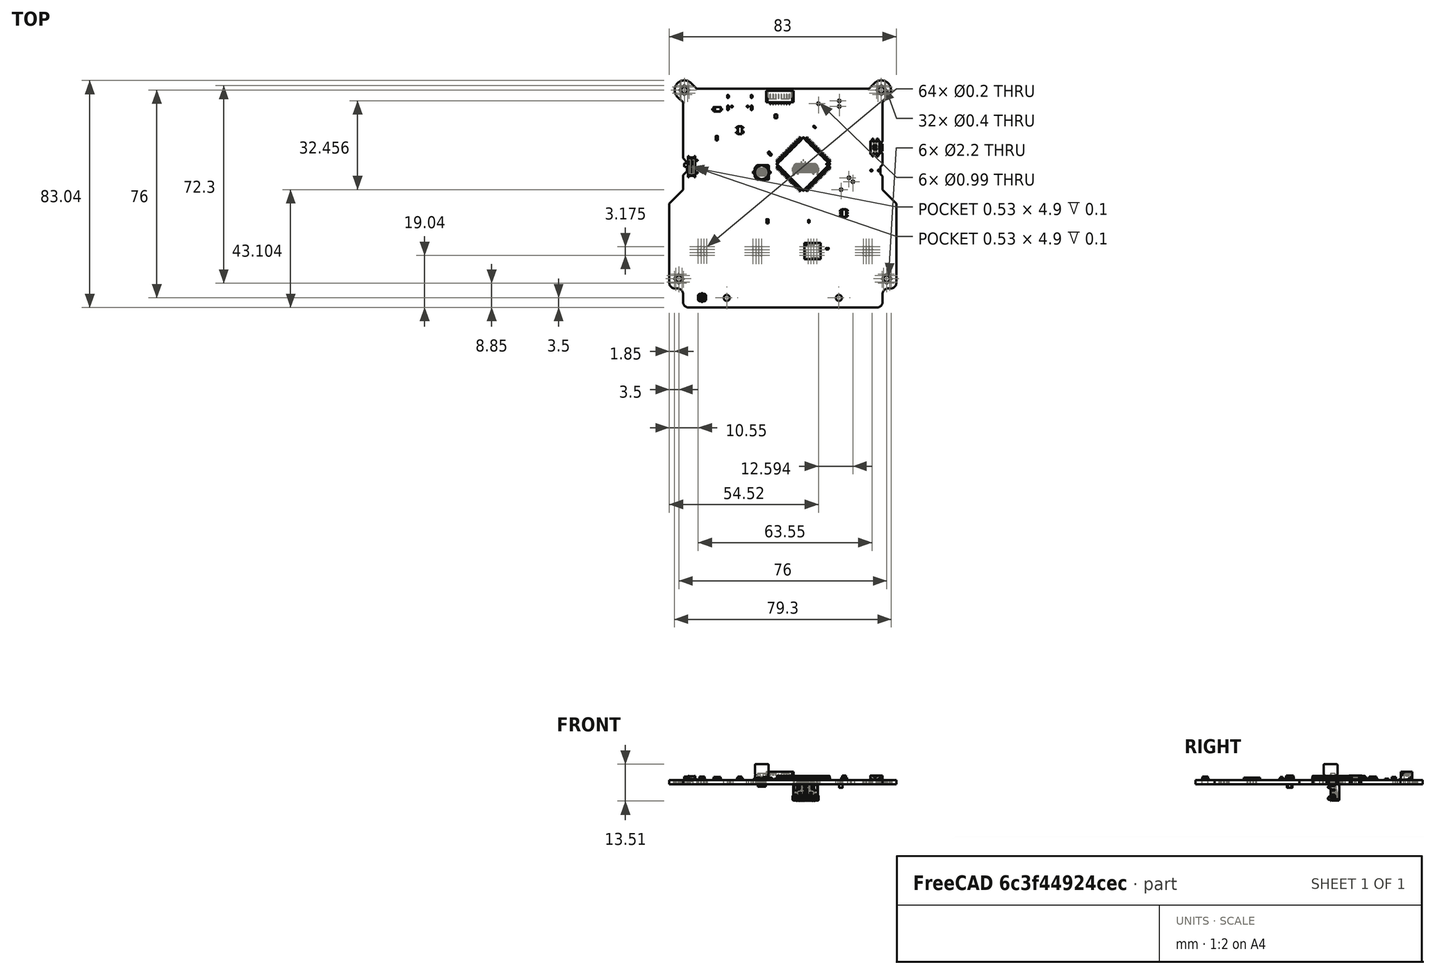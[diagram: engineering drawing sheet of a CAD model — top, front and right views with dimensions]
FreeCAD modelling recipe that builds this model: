
FCSTD DOCUMENT  (FreeCAD 0.20R29410 (Git))
Label: ReLoki_PCB
License: All rights reserved
LicenseURL: http://en.wikipedia.org/wiki/All_rights_reserved
objects: App::Link×261, Part::Feature×83, App::Part×14, PartDesign::CoordinateSystem×1, Sketcher::SketchObject×1
note: 85 computed .brp shape members not serialized (recipe doc carries the construction recipe); baked Part::Feature solids carry a one-line shape summary decoded from their .brp

FEATURE [PartDesign::CoordinateSystem] Local_CS_b912
  AttacherType = Attacher::AttachEngine3D
  MapMode = 2
  Support = -> [X_Axis001]
FEATURE [Part::Feature] Pcb_b912
  Placement = pos=(-58.8,135.6,0) rot=(0,0,1;0rad)
  shape: bbox 83 x 83.04 x 1.58 mm, 187 faces (baked)
FEATURE [Sketcher::SketchObject] PCB_Sketch_b912
  FullyConstrained = false
  sketch-geometry (36):
    g0: LineSegment StartX=43.35 StartY=2 StartZ=0 EndX=43.35 EndY=-0.599999 EndZ=0
    g1: LineSegment StartX=44.2 StartY=6.95 StartZ=0 EndX=44.2 EndY=2.85 EndZ=0
    g2: LineSegment StartX=43.35 StartY=10.4 StartZ=0 EndX=44.2 EndY=11.25 EndZ=0
    g3: LineSegment StartX=43.35 StartY=2 StartZ=0 EndX=44.2 EndY=2.85 EndZ=0
    g4: LineSegment StartX=49.2 StartY=-11.4 StartZ=0 EndX=44.2 EndY=-6.4 EndZ=0
    g5: LineSegment StartX=44.2 StartY=-1.45 StartZ=0 EndX=44.2 EndY=-6.4 EndZ=0
    g6: LineSegment StartX=43.35 StartY=-0.599999 StartZ=0 EndX=44.2 EndY=-1.45 EndZ=0
    g7: LineSegment StartX=-28.8 StartY=-6.4 StartZ=0 EndX=-28.8 EndY=-1.05 EndZ=0
    g8: LineSegment StartX=-23.8 StartY=30.6 StartZ=0 EndX=-25.8 EndY=32.6 EndZ=0
    g9: LineSegment StartX=-33.8 StartY=-11.4 StartZ=0 EndX=-33.8 EndY=-40.4 EndZ=0
    g10: LineSegment StartX=39.2 StartY=30.6 StartZ=0 EndX=41.2 EndY=32.6 EndZ=0
    g11: LineSegment StartX=-33.8 StartY=-11.4 StartZ=0 EndX=-28.8 EndY=-6.4 EndZ=0
    g12: LineSegment StartX=49.2 StartY=-11.4 StartZ=0 EndX=49.2 EndY=-40.4 EndZ=0
    g13: LineSegment StartX=43.35 StartY=10.4 StartZ=0 EndX=43.35 EndY=7.8 EndZ=0
    g14: LineSegment StartX=46.2 StartY=27.6 StartZ=0 EndX=44.2 EndY=25.6 EndZ=0
    g15: LineSegment StartX=-27.3 StartY=3.75 StartZ=0 EndX=-28.8 EndY=5.25 EndZ=0
    g16: LineSegment StartX=-30.8 StartY=-42.4 StartZ=0 EndX=-31.8 EndY=-42.4 EndZ=0
    g17: LineSegment StartX=-23.8 StartY=30.6 StartZ=0 EndX=39.2 EndY=30.6 EndZ=0
    g18: LineSegment StartX=-28.8 StartY=-47.4 StartZ=0 EndX=-28.8 EndY=-44.4 EndZ=0
    g19: LineSegment StartX=-27.3 StartY=0.450001 StartZ=0 EndX=-28.8 EndY=-1.05 EndZ=0
    g20: LineSegment StartX=44.2 StartY=-47.4 StartZ=0 EndX=44.2 EndY=-44.4 EndZ=0
    g21: LineSegment StartX=44.2 StartY=11.25 StartZ=0 EndX=44.2 EndY=25.6 EndZ=0
    g22: LineSegment StartX=-27.3 StartY=3.75 StartZ=0 EndX=-27.3 EndY=0.450001 EndZ=0
    g23: LineSegment StartX=42.2 StartY=-49.4 StartZ=0 EndX=-26.8 EndY=-49.4 EndZ=0
    g24: LineSegment StartX=43.35 StartY=7.8 StartZ=0 EndX=44.2 EndY=6.95 EndZ=0
    g25: LineSegment StartX=-28.8 StartY=25.6 StartZ=0 EndX=-30.8 EndY=27.6 EndZ=0
    g26: LineSegment StartX=47.2 StartY=-42.4 StartZ=0 EndX=46.2 EndY=-42.4 EndZ=0
    g27: LineSegment StartX=-28.8 StartY=5.25 StartZ=0 EndX=-28.8 EndY=25.6 EndZ=0
    g28: ArcOfCircle CenterX=47.2 CenterY=-40.4 CenterZ=0 NormalX=0 NormalY=0 NormalZ=-1 AngleXU=3.14159 Radius=2 StartAngle=0 EndAngle=1.5708
    g29: ArcOfCircle CenterX=-26.8 CenterY=-47.4 CenterZ=0 NormalX=0 NormalY=0 NormalZ=-1 AngleXU=-1.5708 Radius=2 StartAngle=0 EndAngle=1.5708
    g30: ArcOfCircle CenterX=-28.3 CenterY=30.1 CenterZ=0 NormalX=0 NormalY=0 NormalZ=-1 AngleXU=-0.785398 Radius=3.53553 StartAngle=0 EndAngle=3.14159
    g31: ArcOfCircle CenterX=42.2 CenterY=-47.4 CenterZ=0 NormalX=0 NormalY=0 NormalZ=-1 AngleXU=3.14159 Radius=2 StartAngle=0 EndAngle=1.5708
    g32: ArcOfCircle CenterX=-31.8 CenterY=-40.4 CenterZ=0 NormalX=0 NormalY=0 NormalZ=-1 AngleXU=-1.5708 Radius=2 StartAngle=0 EndAngle=1.5708
    g33: ArcOfCircle CenterX=46.2 CenterY=-44.4 CenterZ=0 NormalX=0 NormalY=0 NormalZ=-1 AngleXU=-7.47076e-07 Radius=2 StartAngle=0 EndAngle=1.5708
    g34: ArcOfCircle CenterX=43.7 CenterY=30.1 CenterZ=0 NormalX=0 NormalY=0 NormalZ=-1 AngleXU=0.785398 Radius=3.53553 StartAngle=0 EndAngle=3.14159
    g35: ArcOfCircle CenterX=-30.8 CenterY=-44.4 CenterZ=0 NormalX=0 NormalY=0 NormalZ=-1 AngleXU=1.5708 Radius=2 StartAngle=0 EndAngle=1.5708
  constraints (36):
    c: Coincident(g9,g32)
    c: Coincident(g9,g11)
    c: Coincident(g16,g32)
    c: Coincident(g16,g35)
    c: Coincident(g25,g30)
    c: Coincident(g18,g29)
    c: Coincident(g18,g35)
    c: Coincident(g7,g11)
    c: Coincident(g7,g19)
    c: Coincident(g15,g27)
    c: Coincident(g25,g27)
    c: Coincident(g19,g22)
    c: Coincident(g15,g22)
    c: Coincident(g23,g29)
    c: Coincident(g8,g30)
    c: Coincident(g8,g17)
    c: Coincident(g10,g17)
    c: Coincident(g10,g34)
    c: Coincident(g23,g31)
    c: Coincident(g0,g6)
    c: Coincident(g0,g3)
    c: Coincident(g13,g24)
    c: Coincident(g2,g13)
    c: Coincident(g20,g31)
    c: Coincident(g20,g33)
    c: Coincident(g4,g5)
    c: Coincident(g5,g6)
    c: Coincident(g1,g3)
    c: Coincident(g1,g24)
    c: Coincident(g2,g21)
    c: Coincident(g14,g21)
    c: Coincident(g26,g33)
    c: Coincident(g14,g34)
    c: Coincident(g26,g28)
    c: Coincident(g12,g28)
    c: Coincident(g4,g12)
FEATURE [Part::Feature] Shape  label="R14_R_0402_1005Metric_de650128e65b"
  Placement = pos=(17.2,-17.91,0) rot=(0,0,-1;1.5708rad)
  shape: bbox 0.5 x 1 x 0.35 mm, 26 faces (baked)
FEATURE [Part::Feature] Shape001  label="C81_C_0402_1005Metric_8f684d3886a5"
  Placement = pos=(24,-27.92,0) rot=(0,0,1;0rad)
  shape: bbox 1 x 0.5 x 0.5 mm, 28 faces (baked)
FEATURE [App::Link] R14_R_0402_1005Metric_de650128e65b_ln_  label="R74_R_0402_1005Metric_a4a14273bc81"
  LinkPlacement = pos=(6.5,-7.7,0) rot=(0,0,-1;0.785398rad)
  LinkedObject = -> Shape
  Placement = pos=(6.5,-7.7,0) rot=(0,0,-1;0.785398rad)
FEATURE [App::Link] R14_R_0402_1005Metric_de650128e65b_ln_001  label="R54_R_0402_1005Metric_1bb991507df9"
  LinkPlacement = pos=(5.075,-17.885,0) rot=(0,0,-1;1.5708rad)
  LinkedObject = -> Shape
  Placement = pos=(5.075,-17.885,0) rot=(0,0,-1;1.5708rad)
FEATURE [Part::Feature] Shape002  label="U1_LQFP_100_14x14mm_P05mm_23f8fdaca507"
  Placement = pos=(15.2,3.01585,0) rot=(0,0,1;3.92699rad)
  shape: bbox 19.95 x 19.95 x 1.5 mm, 1544 faces (baked)
FEATURE [App::Link] C81_C_0402_1005Metric_8f684d3886a5_ln_  label="C65_C_0402_1005Metric_c0867cacedee"
  LinkPlacement = pos=(21.01,-34.68,0) rot=(0,0,-1;1.5708rad)
  LinkedObject = -> Shape001
  Placement = pos=(21.01,-34.68,0) rot=(0,0,-1;1.5708rad)
FEATURE [App::Link] C81_C_0402_1005Metric_8f684d3886a5_ln_001  label="C141_C_0402_1005Metric_d101c3108a75"
  LinkPlacement = pos=(-20.925,-23.39,0) rot=(0,0,1;1.5708rad)
  LinkedObject = -> Shape001
  Placement = pos=(-20.925,-23.39,0) rot=(0,0,1;1.5708rad)
FEATURE [App::Link] R14_R_0402_1005Metric_de650128e65b_ln_002  label="R76_R_0402_1005Metric_5a17da7a795e"
  LinkPlacement = pos=(8.5,-14.57,0) rot=(0,0,1;1.5708rad)
  LinkedObject = -> Shape
  Placement = pos=(8.5,-14.57,0) rot=(0,0,1;1.5708rad)
FEATURE [App::Link] R14_R_0402_1005Metric_de650128e65b_ln_003  label="R45_R_0402_1005Metric_9db44bebc8a2"
  LinkPlacement = pos=(37.05,-23.375,0) rot=(0,0,1;1.5708rad)
  LinkedObject = -> Shape
  Placement = pos=(37.05,-23.375,0) rot=(0,0,1;1.5708rad)
FEATURE [App::Link] R14_R_0402_1005Metric_de650128e65b_ln_004  label="R30_R_0402_1005Metric_54cea338f5d0"
  LinkPlacement = pos=(33.8625,14.25,0) rot=(0,0,1;3.14159rad)
  LinkedObject = -> Shape
  Placement = pos=(33.8625,14.25,0) rot=(0,0,1;3.14159rad)
FEATURE [App::Link] R14_R_0402_1005Metric_de650128e65b_ln_005  label="R80_R_0402_1005Metric_603352afcd9c"
  LinkPlacement = pos=(28.9375,-17.86,0) rot=(0,0,-1;1.5708rad)
  LinkedObject = -> Shape
  Placement = pos=(28.9375,-17.86,0) rot=(0,0,-1;1.5708rad)
FEATURE [Part::Feature] Shape003  label="D13_LED_0603_1608Metric_a9e6ce14452c"
  Placement = pos=(2.075,-17.92,0) rot=(0,0,-1;1.5708rad)
  shape: bbox 0.8 x 1.6 x 1.1 mm, 50 faces (baked)
FEATURE [App::Link] R14_R_0402_1005Metric_de650128e65b_ln_006  label="R25_R_0402_1005Metric_f967b688b800"
  LinkPlacement = pos=(33.8625,16.85,0) rot=(0,0,1;3.14159rad)
  LinkedObject = -> Shape
  Placement = pos=(33.8625,16.85,0) rot=(0,0,1;3.14159rad)
FEATURE [App::Link] C81_C_0402_1005Metric_8f684d3886a5_ln_002  label="C127_C_0402_1005Metric_1b485c7792d8"
  LinkPlacement = pos=(-21.25,-34.67,0) rot=(0,0,-1;1.5708rad)
  LinkedObject = -> Shape001
  Placement = pos=(-21.25,-34.67,0) rot=(0,0,-1;1.5708rad)
FEATURE [App::Link] D13_LED_0603_1608Metric_a9e6ce14452c_ln_  label="D14_LED_0603_1608Metric_ef9f26dd3791"
  LinkPlacement = pos=(0.374999,-17.92,0) rot=(0,0,-1;1.5708rad)
  LinkedObject = -> Shape003
  Placement = pos=(0.374999,-17.92,0) rot=(0,0,-1;1.5708rad)
FEATURE [App::Link] C81_C_0402_1005Metric_8f684d3886a5_ln_003  label="C17_C_0402_1005Metric_0b858d9f6a69"
  LinkPlacement = pos=(22.3394,11.9894,0) rot=(0,0,1;0.785398rad)
  LinkedObject = -> Shape001
  Placement = pos=(22.3394,11.9894,0) rot=(0,0,1;0.785398rad)
FEATURE [App::Link] R14_R_0402_1005Metric_de650128e65b_ln_007  label="R8_R_0402_1005Metric_1ff775f01767"
  LinkPlacement = pos=(34.775,-17.91,0) rot=(0,0,1;1.5708rad)
  LinkedObject = -> Shape
  Placement = pos=(34.775,-17.91,0) rot=(0,0,1;1.5708rad)
FEATURE [App::Link] C81_C_0402_1005Metric_8f684d3886a5_ln_004  label="C102_C_0402_1005Metric_637c617e709d"
  LinkPlacement = pos=(0.324999,-33.2,0) rot=(0,0,1;0rad)
  LinkedObject = -> Shape001
  Placement = pos=(0.324999,-33.2,0) rot=(0,0,1;0rad)
FEATURE [App::Link] D13_LED_0603_1608Metric_a9e6ce14452c_ln_001  label="D10_LED_0603_1608Metric_a73bad670425"
  LinkPlacement = pos=(40.65,-17.9325,0) rot=(0,0,-1;1.5708rad)
  LinkedObject = -> Shape003
  Placement = pos=(40.65,-17.9325,0) rot=(0,0,-1;1.5708rad)
FEATURE [App::Link] C81_C_0402_1005Metric_8f684d3886a5_ln_005  label="C28_C_0402_1005Metric_d3135e10789d"
  LinkPlacement = pos=(9.75204,-6.68211,0) rot=(0,0,1;3.92699rad)
  LinkedObject = -> Shape001
  Placement = pos=(9.75204,-6.68211,0) rot=(0,0,1;3.92699rad)
FEATURE [App::Link] R14_R_0402_1005Metric_de650128e65b_ln_008  label="R2_R_0402_1005Metric_00b5c8fd95a4"
  LinkPlacement = pos=(34.1725,23,0) rot=(0,0,1;3.14159rad)
  LinkedObject = -> Shape
  Placement = pos=(34.1725,23,0) rot=(0,0,1;3.14159rad)
FEATURE [App::Link] R14_R_0402_1005Metric_de650128e65b_ln_009  label="R63_R_0402_1005Metric_3ae226b5d65f"
  LinkPlacement = pos=(-27.375,-28.495,0) rot=(0,0,1;1.5708rad)
  LinkedObject = -> Shape
  Placement = pos=(-27.375,-28.495,0) rot=(0,0,1;1.5708rad)
FEATURE [App::Link] C81_C_0402_1005Metric_8f684d3886a5_ln_006  label="C149_C_0402_1005Metric_444c0c827598"
  LinkPlacement = pos=(26.7375,-13.75,0) rot=(0,0,1;3.14159rad)
  LinkedObject = -> Shape001
  Placement = pos=(26.7375,-13.75,0) rot=(0,0,1;3.14159rad)
FEATURE [App::Link] R14_R_0402_1005Metric_de650128e65b_ln_010  label="R50_R_0402_1005Metric_d7a9ffa530aa"
  LinkPlacement = pos=(11.235,-24.56,0) rot=(0,0,1;3.14159rad)
  LinkedObject = -> Shape
  Placement = pos=(11.235,-24.56,0) rot=(0,0,1;3.14159rad)
FEATURE [App::Link] R14_R_0402_1005Metric_de650128e65b_ln_011  label="R46_R_0402_1005Metric_4825f84f8d7c"
  LinkPlacement = pos=(25.15,-17.88,0) rot=(0,0,-1;1.5708rad)
  LinkedObject = -> Shape
  Placement = pos=(25.15,-17.88,0) rot=(0,0,-1;1.5708rad)
FEATURE [App::Link] C81_C_0402_1005Metric_8f684d3886a5_ln_007  label="C73_C_0402_1005Metric_c875b8a4be27"
  LinkPlacement = pos=(24,-31.6,0) rot=(0,0,1;0rad)
  LinkedObject = -> Shape001
  Placement = pos=(24,-31.6,0) rot=(0,0,1;0rad)
FEATURE [App::Link] C81_C_0402_1005Metric_8f684d3886a5_ln_008  label="C134_C_0402_1005Metric_39d0dd4ab5a3"
  LinkPlacement = pos=(-16.2,-30.56,0) rot=(0,0,1;0rad)
  LinkedObject = -> Shape001
  Placement = pos=(-16.2,-30.56,0) rot=(0,0,1;0rad)
FEATURE [App::Link] C81_C_0402_1005Metric_8f684d3886a5_ln_009  label="C151_C_0402_1005Metric_d977a6f65422"
  LinkPlacement = pos=(8.31059,10.9394,0) rot=(0,0,1;2.35619rad)
  LinkedObject = -> Shape001
  Placement = pos=(8.31059,10.9394,0) rot=(0,0,1;2.35619rad)
FEATURE [Part::Feature] Shape004  label="D18_SOT_143_b0c1ef25a24b"
  Placement = pos=(-8.03,15.4398,0) rot=(0,0,1;3.14159rad)
  shape: bbox 2.8 x 2.9 x 1.2 mm, 94 faces (baked)
FEATURE [App::Link] R14_R_0402_1005Metric_de650128e65b_ln_012  label="R57_R_0402_1005Metric_3c6d5dbffcd9"
  LinkPlacement = pos=(-9.325,-32.96,0) rot=(0,0,1;1.5708rad)
  LinkedObject = -> Shape
  Placement = pos=(-9.325,-32.96,0) rot=(0,0,1;1.5708rad)
FEATURE [Part::Feature] Shape005  label="C11_C_0603_1608Metric_4ead5bbb98ed"
  Placement = pos=(-16.45,12.525,0) rot=(0,0,1;1.5708rad)
  shape: bbox 0.8 x 1.6 x 0.8 mm, 28 faces (baked)
FEATURE [Part::Feature] Shape006  label="D20_SOT_886_1dd8b907bd9e"
  Placement = pos=(5.16,20.4898,0) rot=(0,0,1;3.14159rad)
  shape: bbox 1 x 1.45 x 0.52 mm, 38 faces (baked)
FEATURE [Part::Feature] Part__Feature  label="part"
  shape: bbox 0.1003 x 0.1003 x 0.003 mm, 3 faces (baked)
FEATURE [Part::Feature] Part__Feature001  label="part001"
  shape: bbox 2.006 x 1.194 x 0.654 mm, 6 faces (baked)
FEATURE [Part::Feature] Part__Feature002  label="part002"
  shape: bbox 0.508 x 0.99 x 0.006 mm, 6 faces (baked)
FEATURE [Part::Feature] Part__Feature003  label="part003"
  shape: bbox 0.508 x 0.99 x 0.006 mm, 6 faces (baked)
FEATURE [App::Part] part  label="Y2_part004_ffd9eb1ad46b[2]"
  Group = -> [Part__Feature,Part__Feature001,Part__Feature002,Part__Feature003]
  Origin = -> Origin008
  Placement = pos=(3.84444,-0.965614,0) rot=(0,0,1;2.35619rad)
FEATURE [App::Link] C81_C_0402_1005Metric_8f684d3886a5_ln_010  label="C146_C_0402_1005Metric_f6a4e29ba07c"
  LinkPlacement = pos=(9.65,-14.57,0) rot=(0,0,1;1.5708rad)
  LinkedObject = -> Shape001
  Placement = pos=(9.65,-14.57,0) rot=(0,0,1;1.5708rad)
FEATURE [App::Link] C81_C_0402_1005Metric_8f684d3886a5_ln_011  label="C29_C_0402_1005Metric_72a100fbd820"
  LinkPlacement = pos=(20.1394,14.1894,0) rot=(0,0,1;0.785398rad)
  LinkedObject = -> Shape001
  Placement = pos=(20.1394,14.1894,0) rot=(0,0,1;0.785398rad)
FEATURE [App::Link] C81_C_0402_1005Metric_8f684d3886a5_ln_012  label="C130_C_0402_1005Metric_e2b8032ed5ab"
  LinkPlacement = pos=(-19.775,-33.2,0) rot=(0,0,1;0rad)
  LinkedObject = -> Shape001
  Placement = pos=(-19.775,-33.2,0) rot=(0,0,1;0rad)
FEATURE [App::Link] R14_R_0402_1005Metric_de650128e65b_ln_013  label="R37_R_0402_1005Metric_928ee907d34c"
  LinkPlacement = pos=(-18.875,0.890001,0) rot=(0,0,-1;1.5708rad)
  LinkedObject = -> Shape
  Placement = pos=(-18.875,0.890001,0) rot=(0,0,-1;1.5708rad)
FEATURE [Part::Feature] Part__Feature004  label="NONE"
  Placement = pos=(0,-11.5395,4.33352) rot=(0,1,0;1.5708rad)
  shape: bbox 9.583 x 4.163 x 7.533 mm, 1427 faces (baked)
FEATURE [Part::Feature] Part__Feature005  label="ÇÐ³ý-À­Éì2"
  Placement = pos=(0,-11.5395,4.33352) rot=(0,1,0;1.5708rad)
  shape: bbox 7.055 x 2.035 x 7.135 mm, 548 faces (baked)
FEATURE [App::Part] USB4105_15_A  label="J7_USB4105-15-A_0d4446cf3e35[2]"
  Group = -> [Part__Feature004,Part__Feature005]
  Origin = -> Origin009
  Placement = pos=(7.97,30.4098,0) rot=(0,0.707107,0.707107;3.14159rad)
FEATURE [App::Link] C11_C_0603_1608Metric_4ead5bbb98ed_ln_  label="C117_C_0603_1608Metric_39bd58f4b52f"
  LinkPlacement = pos=(-17.85,-34.735,0) rot=(0,0,-1;1.5708rad)
  LinkedObject = -> Shape005
  Placement = pos=(-17.85,-34.735,0) rot=(0,0,-1;1.5708rad)
FEATURE [App::Link] D13_LED_0603_1608Metric_a9e6ce14452c_ln_002  label="D2_LED_0603_1608Metric_1ebbf72df7e2"
  LinkPlacement = pos=(36.9125,23,0) rot=(0,0,1;0rad)
  LinkedObject = -> Shape003
  Placement = pos=(36.9125,23,0) rot=(0,0,1;0rad)
FEATURE [App::Link] C81_C_0402_1005Metric_8f684d3886a5_ln_013  label="C9_C_0402_1005Metric_4d000169be0c"
  LinkPlacement = pos=(2.75,-3.05,0) rot=(0,0,1;0.785398rad)
  LinkedObject = -> Shape001
  Placement = pos=(2.75,-3.05,0) rot=(0,0,1;0.785398rad)
FEATURE [Part::Feature] Shape007  label="SW3_Fusion_sp_02c466c8c368"
  Placement = pos=(-25.3,2.1,0) rot=(0,0,-1;1.5708rad)
  shape: bbox 5 x 7.7 x 2 mm, 141 faces (baked)
FEATURE [App::Link] D13_LED_0603_1608Metric_a9e6ce14452c_ln_003  label="D4_LED_0603_1608Metric_99efae4c4b30"
  LinkPlacement = pos=(36.9125,19.2,0) rot=(0,0,1;0rad)
  LinkedObject = -> Shape003
  Placement = pos=(36.9125,19.2,0) rot=(0,0,1;0rad)
FEATURE [App::Link] R14_R_0402_1005Metric_de650128e65b_ln_014  label="R43_R_0402_1005Metric_da46058e0372"
  LinkPlacement = pos=(42.35,-15.28,0) rot=(0,0,1;1.5708rad)
  LinkedObject = -> Shape
  Placement = pos=(42.35,-15.28,0) rot=(0,0,1;1.5708rad)
FEATURE [App::Link] R14_R_0402_1005Metric_de650128e65b_ln_015  label="R47_R_0402_1005Metric_771e28319039"
  LinkPlacement = pos=(12.85,-28.5,0) rot=(0,0,1;1.5708rad)
  LinkedObject = -> Shape
  Placement = pos=(12.85,-28.5,0) rot=(0,0,1;1.5708rad)
FEATURE [Part::Feature] Shape008  label="SW2_EVQPU-LC-02K v4_ac6ec0e7e283[2]"
  Placement = pos=(41.45,9.1,0) rot=(0.57735,0.57735,0.57735;2.0944rad)
  shape: bbox 4.542 x 6.402 x 2.183 mm, 270 faces (baked)
FEATURE [App::Link] D13_LED_0603_1608Metric_a9e6ce14452c_ln_004  label="D16_LED_0603_1608Metric_2864ecb3f3d8"
  LinkPlacement = pos=(-19.725,-17.92,0) rot=(0,0,-1;1.5708rad)
  LinkedObject = -> Shape003
  Placement = pos=(-19.725,-17.92,0) rot=(0,0,-1;1.5708rad)
FEATURE [App::Link] C81_C_0402_1005Metric_8f684d3886a5_ln_014  label="C88_C_0402_1005Metric_34164e20f501"
  LinkPlacement = pos=(-8.855,-28.96,0) rot=(0,0,1;3.14159rad)
  LinkedObject = -> Shape001
  Placement = pos=(-8.855,-28.96,0) rot=(0,0,1;3.14159rad)
FEATURE [App::Link] R14_R_0402_1005Metric_de650128e65b_ln_016  label="R73_R_0402_1005Metric_d5867035460b"
  LinkPlacement = pos=(-8.59,12.0898,0) rot=(0,0,-1;1.5708rad)
  LinkedObject = -> Shape
  Placement = pos=(-8.59,12.0898,0) rot=(0,0,-1;1.5708rad)
FEATURE [Part::Feature] Shape009  label="U5_QFN40P600X600X90-48_Nordic_Semiconductor_QFN48_2cf8b7c55fc9"
  Placement = pos=(18.525,-28.785,0) rot=(0,0,1;0rad)
  shape: bbox 6.02 x 6.02 x 0.9 mm, 302 faces (baked)
FEATURE [App::Link] R14_R_0402_1005Metric_de650128e65b_ln_017  label="R15_R_0402_1005Metric_1a5054cc167c"
  LinkPlacement = pos=(-2.95,-17.9,0) rot=(0,0,-1;1.5708rad)
  LinkedObject = -> Shape
  Placement = pos=(-2.95,-17.9,0) rot=(0,0,-1;1.5708rad)
FEATURE [App::Link] C81_C_0402_1005Metric_8f684d3886a5_ln_015  label="C86_C_0402_1005Metric_aac071f58c84"
  LinkPlacement = pos=(18.375,-38.03,0) rot=(0,0,-1;1.5708rad)
  LinkedObject = -> Shape001
  Placement = pos=(18.375,-38.03,0) rot=(0,0,-1;1.5708rad)
FEATURE [App::Link] C81_C_0402_1005Metric_8f684d3886a5_ln_016  label="C150_C_0402_1005Metric_d87a535d9fed"
  LinkPlacement = pos=(26,-1.3,0) rot=(0,0,-1;0.785398rad)
  LinkedObject = -> Shape001
  Placement = pos=(26,-1.3,0) rot=(0,0,-1;0.785398rad)
FEATURE [App::Link] R14_R_0402_1005Metric_de650128e65b_ln_018  label="R23_R_0402_1005Metric_31860b2061f3"
  LinkPlacement = pos=(36.3,3.35,0) rot=(0,0,1;0rad)
  LinkedObject = -> Shape
  Placement = pos=(36.3,3.35,0) rot=(0,0,1;0rad)
FEATURE [Part::Feature] Part__Feature006  label="─σ≥αδⁿ"
  shape: bbox 1.5 x 1.5 x 0.5 mm, 6 faces (baked)
FEATURE [Part::Feature] Part__Feature007  label="─σ≥αδⁿ_2"
  Placement = pos=(-0.55,-0.5,0.5) rot=(0,0,1;0rad)
  shape: bbox 0.4 x 0.3 x 0.05 mm, 7 faces (baked)
FEATURE [Part::Feature] Part__Feature008  label="─σ≥αδⁿ_3"
  Placement = pos=(-0.55,-1e-15,0.5) rot=(0,0,1;0rad)
  shape: bbox 0.4 x 0.25 x 0.05 mm, 6 faces (baked)
FEATURE [Part::Feature] Part__Feature009  label="─σ≥αδⁿ_4"
  Placement = pos=(-0.55,0.5,0.5) rot=(0,0,1;0rad)
  shape: bbox 0.4 x 0.3 x 0.05 mm, 6 faces (baked)
FEATURE [Part::Feature] Part__Feature010  label="─σ≥αδⁿ_005"
  Placement = pos=(0.55,-0.5,0.5) rot=(0,0,1;0rad)
  shape: bbox 0.4 x 0.3 x 0.05 mm, 6 faces (baked)
FEATURE [Part::Feature] Part__Feature011  label="─σ≥αδⁿ_006"
  Placement = pos=(0.55,0.5,0.5) rot=(0,0,1;0rad)
  shape: bbox 0.4 x 0.3 x 0.05 mm, 6 faces (baked)
FEATURE [Part::Feature] Part__Feature012  label="─σ≥αδⁿ_007"
  Placement = pos=(0.55,0,0.5) rot=(0,0,1;0rad)
  shape: bbox 0.4 x 0.25 x 0.05 mm, 6 faces (baked)
FEATURE [Part::Feature] Part__Feature013  label="─σ≥αδⁿ_5"
  Placement = pos=(0,-0.525,0.5) rot=(0,0,-1;1.5708rad)
  shape: bbox 0.35 x 0.45 x 0.05 mm, 6 faces (baked)
FEATURE [Part::Feature] Part__Feature014  label="─σ≥αδⁿ_008"
  Placement = pos=(0,0.525,0.5) rot=(0,0,-1;1.5708rad)
  shape: bbox 0.35 x 0.45 x 0.05 mm, 6 faces (baked)
FEATURE [Part::Feature] Part__Feature015  label="─σ≥αδⁿ_6"
  Placement = pos=(-0.5,-0.5,-0.005) rot=(0,0,1;0rad)
  shape: bbox 0.25 x 0.25 x 0.1 mm, 4 faces (baked)
FEATURE [App::Part] User_Library_uqfn8  label="U12_User Library-uqfn8_8f146cca9007"
  Group = -> [Part__Feature006,Part__Feature007,Part__Feature008,Part__Feature009,Part__Feature010,Part__Feature011,Part__Feature012,Part__Feature013,Part__Feature014,Part__Feature015]
  Origin = -> Origin010
  Placement = pos=(-4.45,-7,0.51) rot=(0,1,0;3.14159rad)
FEATURE [Part::Feature] Shape010  label="L1_L_0402_1005Metric_5998b2d09642"
  Placement = pos=(19.302,16.5904,0) rot=(0,0,-1;0.785398rad)
  shape: bbox 1.061 x 1.061 x 0.5 mm, 28 faces (baked)
FEATURE [App::Link] R14_R_0402_1005Metric_de650128e65b_ln_019  label="R60_R_0402_1005Metric_0914d451b9f9"
  LinkPlacement = pos=(0.374999,-15.28,0) rot=(0,0,1;1.5708rad)
  LinkedObject = -> Shape
  Placement = pos=(0.374999,-15.28,0) rot=(0,0,1;1.5708rad)
FEATURE [App::Link] C81_C_0402_1005Metric_8f684d3886a5_ln_017  label="C100_C_0402_1005Metric_557190ddb8d7"
  LinkPlacement = pos=(-7.695,-31.36,0) rot=(0,0,1;3.14159rad)
  LinkedObject = -> Shape001
  Placement = pos=(-7.695,-31.36,0) rot=(0,0,1;3.14159rad)
FEATURE [App::Link] C81_C_0402_1005Metric_8f684d3886a5_ln_018  label="C68_C_0402_1005Metric_135fffc550a4"
  LinkPlacement = pos=(14,-32.915,0) rot=(0,0,1;1.5708rad)
  LinkedObject = -> Shape001
  Placement = pos=(14,-32.915,0) rot=(0,0,1;1.5708rad)
FEATURE [App::Link] C81_C_0402_1005Metric_8f684d3886a5_ln_019  label="C109_C_0402_1005Metric_56ac115547da"
  LinkPlacement = pos=(3.9,-27.92,0) rot=(0,0,1;0rad)
  LinkedObject = -> Shape001
  Placement = pos=(3.9,-27.92,0) rot=(0,0,1;0rad)
FEATURE [App::Link] C81_C_0402_1005Metric_8f684d3886a5_ln_020  label="C69_C_0402_1005Metric_3595023d93e6"
  LinkPlacement = pos=(23.995,-29.3,0) rot=(0,0,1;0rad)
  LinkedObject = -> Shape001
  Placement = pos=(23.995,-29.3,0) rot=(0,0,1;0rad)
FEATURE [App::Link] C81_C_0402_1005Metric_8f684d3886a5_ln_021  label="C114_C_0402_1005Metric_f1c06565e7f7"
  LinkPlacement = pos=(-1.75,-38.03,0) rot=(0,0,-1;1.5708rad)
  LinkedObject = -> Shape001
  Placement = pos=(-1.75,-38.03,0) rot=(0,0,-1;1.5708rad)
FEATURE [App::Link] C11_C_0603_1608Metric_4ead5bbb98ed_ln_001  label="C61_C_0603_1608Metric_6e7d13db5697"
  LinkPlacement = pos=(22.325,-34.735,0) rot=(0,0,-1;1.5708rad)
  LinkedObject = -> Shape005
  Placement = pos=(22.325,-34.735,0) rot=(0,0,-1;1.5708rad)
FEATURE [App::Link] R14_R_0402_1005Metric_de650128e65b_ln_020  label="R66_R_0402_1005Metric_6d20dbbd573a"
  LinkPlacement = pos=(-28.965,-24.56,0) rot=(0,0,1;3.14159rad)
  LinkedObject = -> Shape
  Placement = pos=(-28.965,-24.56,0) rot=(0,0,1;3.14159rad)
FEATURE [App::Link] D20_SOT_886_1dd8b907bd9e_ln_  label="D6_SOT_886_d59cf476959a"
  LinkPlacement = pos=(28.03,21.1348,0) rot=(0,0,1;3.14159rad)
  LinkedObject = -> Shape006
  Placement = pos=(28.03,21.1348,0) rot=(0,0,1;3.14159rad)
FEATURE [App::Link] C81_C_0402_1005Metric_8f684d3886a5_ln_022  label="C93_C_0402_1005Metric_fb1c744605cf"
  LinkPlacement = pos=(0.899999,-34.68,0) rot=(0,0,-1;1.5708rad)
  LinkedObject = -> Shape001
  Placement = pos=(0.899999,-34.68,0) rot=(0,0,-1;1.5708rad)
FEATURE [App::Link] C81_C_0402_1005Metric_8f684d3886a5_ln_023  label="C59_C_0402_1005Metric_e9a5220afd4d"
  LinkPlacement = pos=(37.275,-38.03,0) rot=(0,0,-1;1.5708rad)
  LinkedObject = -> Shape001
  Placement = pos=(37.275,-38.03,0) rot=(0,0,-1;1.5708rad)
FEATURE [App::Link] C81_C_0402_1005Metric_8f684d3886a5_ln_024  label="C98_C_0402_1005Metric_8185cb620f1a"
  LinkPlacement = pos=(-7.705,-32.46,0) rot=(0,0,1;0rad)
  LinkedObject = -> Shape001
  Placement = pos=(-7.705,-32.46,0) rot=(0,0,1;0rad)
FEATURE [App::Link] D13_LED_0603_1608Metric_a9e6ce14452c_ln_005  label="D8_LED_0603_1608Metric_4827e450632c"
  LinkPlacement = pos=(-18.9,3.69,0) rot=(0,0,1;1.5708rad)
  LinkedObject = -> Shape003
  Placement = pos=(-18.9,3.69,0) rot=(0,0,1;1.5708rad)
FEATURE [App::Link] C81_C_0402_1005Metric_8f684d3886a5_ln_025  label="C32_C_0402_1005Metric_cd6915d46d3a"
  LinkPlacement = pos=(31.415,-29.015,0) rot=(0,0,1;3.14159rad)
  LinkedObject = -> Shape001
  Placement = pos=(31.415,-29.015,0) rot=(0,0,1;3.14159rad)
FEATURE [App::Link] R14_R_0402_1005Metric_de650128e65b_ln_021  label="R70_R_0402_1005Metric_4c9a27012615"
  LinkPlacement = pos=(-6.78,18.5398,0) rot=(0,0,-1;1.5708rad)
  LinkedObject = -> Shape
  Placement = pos=(-6.78,18.5398,0) rot=(0,0,-1;1.5708rad)
FEATURE [App::Link] C81_C_0402_1005Metric_8f684d3886a5_ln_026  label="C38_C_0402_1005Metric_92217313c114"
  LinkPlacement = pos=(36,-23.385,0) rot=(0,0,1;1.5708rad)
  LinkedObject = -> Shape001
  Placement = pos=(36,-23.385,0) rot=(0,0,1;1.5708rad)
FEATURE [App::Link] R14_R_0402_1005Metric_de650128e65b_ln_022  label="R35_R_0402_1005Metric_ec15f12d3b37"
  LinkPlacement = pos=(-24.95,12.14,0) rot=(0,0,1;1.5708rad)
  LinkedObject = -> Shape
  Placement = pos=(-24.95,12.14,0) rot=(0,0,1;1.5708rad)
FEATURE [App::Link] R14_R_0402_1005Metric_de650128e65b_ln_023  label="R39_R_0402_1005Metric_992b80647fb1"
  LinkPlacement = pos=(33.05,-28.5,0) rot=(0,0,1;1.5708rad)
  LinkedObject = -> Shape
  Placement = pos=(33.05,-28.5,0) rot=(0,0,1;1.5708rad)
FEATURE [App::Link] C11_C_0603_1608Metric_4ead5bbb98ed_ln_002  label="C1_C_0603_1608Metric_eaafb3855c50"
  LinkPlacement = pos=(19.575,21.1798,0) rot=(0,0,1;3.14159rad)
  LinkedObject = -> Shape005
  Placement = pos=(19.575,21.1798,0) rot=(0,0,1;3.14159rad)
FEATURE [App::Link] C81_C_0402_1005Metric_8f684d3886a5_ln_027  label="C84_C_0402_1005Metric_a1e1eb2d7525"
  LinkPlacement = pos=(14.725,-23.375,0) rot=(0,0,1;1.5708rad)
  LinkedObject = -> Shape001
  Placement = pos=(14.725,-23.375,0) rot=(0,0,1;1.5708rad)
FEATURE [Part::Feature] Shape011  label="D17_D_SOD_123F_4ad0e2d0f864"
  Placement = pos=(-16.28,23.0898,0) rot=(0,0,1;0rad)
  shape: bbox 3.5 x 1.6 x 1.1 mm, 27 faces (baked)
FEATURE [Part::Feature] Shape012  label="J6_U.FL_Hirose_U.FL-R-SMT-1_Vertical_4116725bd3ca"
  Placement = pos=(-21.825,-45.785,0) rot=(0,0,-1;1.5708rad)
  shape: bbox 3 x 3.1 x 1.25 mm, 46 faces (baked)
FEATURE [App::Link] C81_C_0402_1005Metric_8f684d3886a5_ln_028  label="C107_C_0402_1005Metric_c4881c660e8b"
  LinkPlacement = pos=(-8.85,-26.81,0) rot=(0,0,1;3.14159rad)
  LinkedObject = -> Shape001
  Placement = pos=(-8.85,-26.81,0) rot=(0,0,1;3.14159rad)
FEATURE [App::Link] C81_C_0402_1005Metric_8f684d3886a5_ln_029  label="C72_C_0402_1005Metric_3776bdc644e2"
  LinkPlacement = pos=(12.4,-31.36,0) rot=(0,0,1;3.14159rad)
  LinkedObject = -> Shape001
  Placement = pos=(12.4,-31.36,0) rot=(0,0,1;3.14159rad)
FEATURE [App::Link] C81_C_0402_1005Metric_8f684d3886a5_ln_030  label="C51_C_0402_1005Metric_91736355e4be"
  LinkPlacement = pos=(31.4,-26.81,0) rot=(0,0,1;3.14159rad)
  LinkedObject = -> Shape001
  Placement = pos=(31.4,-26.81,0) rot=(0,0,1;3.14159rad)
FEATURE [App::Link] R14_R_0402_1005Metric_de650128e65b_ln_024  label="R42_R_0402_1005Metric_e76268048612"
  LinkPlacement = pos=(31.39,-24.56,0) rot=(0,0,1;3.14159rad)
  LinkedObject = -> Shape
  Placement = pos=(31.39,-24.56,0) rot=(0,0,1;3.14159rad)
FEATURE [App::Link] D13_LED_0603_1608Metric_a9e6ce14452c_ln_006  label="D12_LED_0603_1608Metric_0a28de12d8d7"
  LinkPlacement = pos=(20.475,-17.92,0) rot=(0,0,-1;1.5708rad)
  LinkedObject = -> Shape003
  Placement = pos=(20.475,-17.92,0) rot=(0,0,-1;1.5708rad)
FEATURE [App::Link] C81_C_0402_1005Metric_8f684d3886a5_ln_031  label="C54_C_0402_1005Metric_39b98724dd97"
  LinkPlacement = pos=(32.6,-30.26,0) rot=(0,0,1;3.14159rad)
  LinkedObject = -> Shape001
  Placement = pos=(32.6,-30.26,0) rot=(0,0,1;3.14159rad)
FEATURE [App::Link] C81_C_0402_1005Metric_8f684d3886a5_ln_032  label="C78_C_0402_1005Metric_ab463bb9c96b"
  LinkPlacement = pos=(23.995,-30.57,0) rot=(0,0,1;0rad)
  LinkedObject = -> Shape001
  Placement = pos=(23.995,-30.57,0) rot=(0,0,1;0rad)
FEATURE [App::Link] C81_C_0402_1005Metric_8f684d3886a5_ln_033  label="C97_C_0402_1005Metric_6ab874785eab"
  LinkPlacement = pos=(3.9,-29.3,0) rot=(0,0,1;0rad)
  LinkedObject = -> Shape001
  Placement = pos=(3.9,-29.3,0) rot=(0,0,1;0rad)
FEATURE [App::Link] C81_C_0402_1005Metric_8f684d3886a5_ln_034  label="C120_C_0402_1005Metric_397f24707a76"
  LinkPlacement = pos=(-30.575,-30.46,0) rot=(0,0,-1;1.5708rad)
  LinkedObject = -> Shape001
  Placement = pos=(-30.575,-30.46,0) rot=(0,0,-1;1.5708rad)
FEATURE [App::Link] C81_C_0402_1005Metric_8f684d3886a5_ln_035  label="C115_C_0402_1005Metric_f89cd3243a66"
  LinkPlacement = pos=(-3.05,-38.03,0) rot=(0,0,-1;1.5708rad)
  LinkedObject = -> Shape001
  Placement = pos=(-3.05,-38.03,0) rot=(0,0,-1;1.5708rad)
FEATURE [App::Link] C81_C_0402_1005Metric_8f684d3886a5_ln_036  label="C113_C_0402_1005Metric_60e4371117a5"
  LinkPlacement = pos=(-0.850001,-23.405,0) rot=(0,0,1;1.5708rad)
  LinkedObject = -> Shape001
  Placement = pos=(-0.850001,-23.405,0) rot=(0,0,1;1.5708rad)
FEATURE [App::Link] J6_U_FL_Hirose_U_FL_R_SMT_1_Vertical_4116725bd3ca_ln_  label="J4_U.FL_Hirose_U.FL-R-SMT-1_Vertical_0db01d2b2d7b"
  LinkPlacement = pos=(18.375,-45.785,0) rot=(0,0,-1;1.5708rad)
  LinkedObject = -> Shape012
  Placement = pos=(18.375,-45.785,0) rot=(0,0,-1;1.5708rad)
FEATURE [App::Link] R14_R_0402_1005Metric_de650128e65b_ln_025  label="R22_R_0402_1005Metric_980955f24782"
  LinkPlacement = pos=(-1.75,-17.9,0) rot=(0,0,-1;1.5708rad)
  LinkedObject = -> Shape
  Placement = pos=(-1.75,-17.9,0) rot=(0,0,-1;1.5708rad)
FEATURE [App::Link] C81_C_0402_1005Metric_8f684d3886a5_ln_037  label="C48_C_0402_1005Metric_8bdf6c26c0f4"
  LinkPlacement = pos=(31.4,-25.71,0) rot=(0,0,1;3.14159rad)
  LinkedObject = -> Shape001
  Placement = pos=(31.4,-25.71,0) rot=(0,0,1;3.14159rad)
FEATURE [App::Link] C81_C_0402_1005Metric_8f684d3886a5_ln_038  label="C16_C_0402_1005Metric_c4d3f523ed00"
  LinkPlacement = pos=(5.79145,9.1,0) rot=(0,0,1;0.785398rad)
  LinkedObject = -> Shape001
  Placement = pos=(5.79145,9.1,0) rot=(0,0,1;0.785398rad)
FEATURE [App::Link] C81_C_0402_1005Metric_8f684d3886a5_ln_039  label="C105_C_0402_1005Metric_da5669578102"
  LinkPlacement = pos=(-1.925,-23.39,0) rot=(0,0,1;1.5708rad)
  LinkedObject = -> Shape001
  Placement = pos=(-1.925,-23.39,0) rot=(0,0,1;1.5708rad)
FEATURE [App::Link] C81_C_0402_1005Metric_8f684d3886a5_ln_040  label="C92_C_0402_1005Metric_81df448325a2"
  LinkPlacement = pos=(-10.475,-30.46,0) rot=(0,0,-1;1.5708rad)
  LinkedObject = -> Shape001
  Placement = pos=(-10.475,-30.46,0) rot=(0,0,-1;1.5708rad)
FEATURE [App::Link] R14_R_0402_1005Metric_de650128e65b_ln_026  label="R78_R_0402_1005Metric_9fc1efc35038"
  LinkPlacement = pos=(-11.15,-11.95,0) rot=(0,0,1;1.5708rad)
  LinkedObject = -> Shape
  Placement = pos=(-11.15,-11.95,0) rot=(0,0,1;1.5708rad)
FEATURE [App::Link] C81_C_0402_1005Metric_8f684d3886a5_ln_041  label="C124_C_0402_1005Metric_ac0d63eab82d"
  LinkPlacement = pos=(-26.2,-32.91,0) rot=(0,0,1;1.5708rad)
  LinkedObject = -> Shape001
  Placement = pos=(-26.2,-32.91,0) rot=(0,0,1;1.5708rad)
FEATURE [App::Link] R14_R_0402_1005Metric_de650128e65b_ln_027  label="R32_R_0402_1005Metric_b124fa7f42c4"
  LinkPlacement = pos=(33.1,11.2,0) rot=(0,0,1;1.5708rad)
  LinkedObject = -> Shape
  Placement = pos=(33.1,11.2,0) rot=(0,0,1;1.5708rad)
FEATURE [App::Link] C81_C_0402_1005Metric_8f684d3886a5_ln_042  label="C74_C_0402_1005Metric_fa95f18dbc6b"
  LinkPlacement = pos=(20.45,-33.21,0) rot=(0,0,1;0rad)
  LinkedObject = -> Shape001
  Placement = pos=(20.45,-33.21,0) rot=(0,0,1;0rad)
FEATURE [App::Link] C81_C_0402_1005Metric_8f684d3886a5_ln_043  label="C135_C_0402_1005Metric_0fc2aea8a6a5"
  LinkPlacement = pos=(-28.975,-26.81,0) rot=(0,0,1;3.14159rad)
  LinkedObject = -> Shape001
  Placement = pos=(-28.975,-26.81,0) rot=(0,0,1;3.14159rad)
FEATURE [App::Link] C81_C_0402_1005Metric_8f684d3886a5_ln_044  label="C22_C_0402_1005Metric_708433e22d88"
  LinkPlacement = pos=(4.41263,10.3573,0) rot=(0,0,1;2.35619rad)
  LinkedObject = -> Shape001
  Placement = pos=(4.41263,10.3573,0) rot=(0,0,1;2.35619rad)
FEATURE [App::Link] R14_R_0402_1005Metric_de650128e65b_ln_028  label="R18_R_0402_1005Metric_16a396d9810f"
  LinkPlacement = pos=(14.8,-17.9,0) rot=(0,0,-1;1.5708rad)
  LinkedObject = -> Shape
  Placement = pos=(14.8,-17.9,0) rot=(0,0,-1;1.5708rad)
FEATURE [App::Link] R14_R_0402_1005Metric_de650128e65b_ln_029  label="R41_R_0402_1005Metric_c37a669f2bd5"
  LinkPlacement = pos=(30.94,-32.965,0) rot=(0,0,1;1.5708rad)
  LinkedObject = -> Shape
  Placement = pos=(30.94,-32.965,0) rot=(0,0,1;1.5708rad)
FEATURE [App::Link] R14_R_0402_1005Metric_de650128e65b_ln_030  label="R29_R_0402_1005Metric_3afbbdb1df1f"
  LinkPlacement = pos=(26.2,21.1798,0) rot=(0,0,-1;1.5708rad)
  LinkedObject = -> Shape
  Placement = pos=(26.2,21.1798,0) rot=(0,0,-1;1.5708rad)
FEATURE [App::Link] D13_LED_0603_1608Metric_a9e6ce14452c_ln_007  label="D9_LED_0603_1608Metric_8b0193c5ac55"
  LinkPlacement = pos=(42.35,-17.92,0) rot=(0,0,-1;1.5708rad)
  LinkedObject = -> Shape003
  Placement = pos=(42.35,-17.92,0) rot=(0,0,-1;1.5708rad)
FEATURE [App::Link] C81_C_0402_1005Metric_8f684d3886a5_ln_045  label="C62_C_0402_1005Metric_694e0b04c4d4"
  LinkPlacement = pos=(16.325,-33.565,0) rot=(0,0,-1;1.5708rad)
  LinkedObject = -> Shape001
  Placement = pos=(16.325,-33.565,0) rot=(0,0,-1;1.5708rad)
FEATURE [App::Link] C81_C_0402_1005Metric_8f684d3886a5_ln_046  label="C30_C_0402_1005Metric_876e4fe13210"
  LinkPlacement = pos=(21.3415,-5.98211,0) rot=(0,0,-1;0.785398rad)
  LinkedObject = -> Shape001
  Placement = pos=(21.3415,-5.98211,0) rot=(0,0,-1;0.785398rad)
FEATURE [App::Link] U5_QFN40P600X600X90_48_Nordic_Semiconductor_QFN48_2cf8b7c55fc9_ln_  label="U7_QFN40P600X600X90-48_Nordic_Semiconductor_QFN48_8e78b246d3da"
  LinkPlacement = pos=(-1.6,-28.785,0) rot=(0,0,1;0rad)
  LinkedObject = -> Shape009
  Placement = pos=(-1.6,-28.785,0) rot=(0,0,1;0rad)
FEATURE [App::Link] C81_C_0402_1005Metric_8f684d3886a5_ln_047  label="C60_C_0402_1005Metric_aa1e40123048"
  LinkPlacement = pos=(11.25,-28.96,0) rot=(0,0,1;3.14159rad)
  LinkedObject = -> Shape001
  Placement = pos=(11.25,-28.96,0) rot=(0,0,1;3.14159rad)
FEATURE [Part::Feature] Part__Feature016  label="C_Elec_5x58"
  shape: bbox 6.985 x 6.828 x 5.8 mm, 38 faces (baked)
FEATURE [Part::Feature] Part__Feature017  label="C_Elec_5x059"
  shape: bbox 0.02 x 0.02 x 0.01 mm, 3 faces (baked)
FEATURE [App::Part] C_Elec_5x58  label="C3_C_Elec_5x060_20e2f45bb341"
  Group = -> [Part__Feature016,Part__Feature017]
  Origin = -> Origin011
  Placement = pos=(-23.35,23.09,0) rot=(0,0,1;3.14159rad)
FEATURE [App::Link] R14_R_0402_1005Metric_de650128e65b_ln_031  label="R68_R_0402_1005Metric_a5c06850edf2"
  LinkPlacement = pos=(-19.725,-15.28,0) rot=(0,0,1;1.5708rad)
  LinkedObject = -> Shape
  Placement = pos=(-19.725,-15.28,0) rot=(0,0,1;1.5708rad)
FEATURE [App::Link] D17_D_SOD_123F_4ad0e2d0f864_ln_  label="D19_D_SOD_123F_431956aee66c"
  LinkPlacement = pos=(12.5,22.6398,0) rot=(0,0,1;3.14159rad)
  LinkedObject = -> Shape011
  Placement = pos=(12.5,22.6398,0) rot=(0,0,1;3.14159rad)
FEATURE [App::Link] C81_C_0402_1005Metric_8f684d3886a5_ln_048  label="C53_C_0402_1005Metric_75c69b60b14a"
  LinkPlacement = pos=(44.21,-27.92,0) rot=(0,0,1;0rad)
  LinkedObject = -> Shape001
  Placement = pos=(44.21,-27.92,0) rot=(0,0,1;0rad)
FEATURE [App::Link] J6_U_FL_Hirose_U_FL_R_SMT_1_Vertical_4116725bd3ca_ln_001  label="J3_U.FL_Hirose_U.FL-R-SMT-1_Vertical_4b589a610575"
  LinkPlacement = pos=(38.575,-45.785,0) rot=(0,0,-1;1.5708rad)
  LinkedObject = -> Shape012
  Placement = pos=(38.575,-45.785,0) rot=(0,0,-1;1.5708rad)
FEATURE [App::Link] R14_R_0402_1005Metric_de650128e65b_ln_032  label="R28_R_0402_1005Metric_5d1a9a8c8929"
  LinkPlacement = pos=(24.84,21.1798,0) rot=(0,0,-1;1.5708rad)
  LinkedObject = -> Shape
  Placement = pos=(24.84,21.1798,0) rot=(0,0,-1;1.5708rad)
FEATURE [App::Link] R14_R_0402_1005Metric_de650128e65b_ln_033  label="R75_R_0402_1005Metric_8dfb7854bf13"
  LinkPlacement = pos=(3.95,-4.3,0) rot=(0,0,1;3.92699rad)
  LinkedObject = -> Shape
  Placement = pos=(3.95,-4.3,0) rot=(0,0,1;3.92699rad)
FEATURE [App::Link] R14_R_0402_1005Metric_de650128e65b_ln_034  label="R72_R_0402_1005Metric_c9014f804070"
  LinkPlacement = pos=(-7.48,12.0898,0) rot=(0,0,-1;1.5708rad)
  LinkedObject = -> Shape
  Placement = pos=(-7.48,12.0898,0) rot=(0,0,-1;1.5708rad)
FEATURE [App::Link] C81_C_0402_1005Metric_8f684d3886a5_ln_049  label="C79_C_0402_1005Metric_845a75a648b1"
  LinkPlacement = pos=(11.255,-26.81,0) rot=(0,0,1;3.14159rad)
  LinkedObject = -> Shape001
  Placement = pos=(11.255,-26.81,0) rot=(0,0,1;3.14159rad)
FEATURE [App::Link] C81_C_0402_1005Metric_8f684d3886a5_ln_050  label="C56_C_0402_1005Metric_7f91b05b7bf3"
  LinkPlacement = pos=(34.95,-23.385,0) rot=(0,0,1;1.5708rad)
  LinkedObject = -> Shape001
  Placement = pos=(34.95,-23.385,0) rot=(0,0,1;1.5708rad)
FEATURE [App::Link] C81_C_0402_1005Metric_8f684d3886a5_ln_051  label="C148_C_0402_1005Metric_6b28c42d5b2b"
  LinkPlacement = pos=(-4.93,-9.2,0) rot=(0,0,1;3.14159rad)
  LinkedObject = -> Shape001
  Placement = pos=(-4.93,-9.2,0) rot=(0,0,1;3.14159rad)
FEATURE [App::Link] R14_R_0402_1005Metric_de650128e65b_ln_035  label="R81_R_0402_1005Metric_ff96f1f161a6"
  LinkPlacement = pos=(-8.85,-17.86,0) rot=(0,0,-1;1.5708rad)
  LinkedObject = -> Shape
  Placement = pos=(-8.85,-17.86,0) rot=(0,0,-1;1.5708rad)
FEATURE [App::Link] R14_R_0402_1005Metric_de650128e65b_ln_036  label="R4_R_0402_1005Metric_f8d67018c139"
  LinkPlacement = pos=(-25.25,-17.9,0) rot=(0,0,1;1.5708rad)
  LinkedObject = -> Shape
  Placement = pos=(-25.25,-17.9,0) rot=(0,0,1;1.5708rad)
FEATURE [App::Link] C81_C_0402_1005Metric_8f684d3886a5_ln_052  label="C144_C_0402_1005Metric_f30e0f9d8192"
  LinkPlacement = pos=(8.18,-20.05,0) rot=(0,0,1;3.14159rad)
  LinkedObject = -> Shape001
  Placement = pos=(8.18,-20.05,0) rot=(0,0,1;3.14159rad)
FEATURE [App::Link] C81_C_0402_1005Metric_8f684d3886a5_ln_053  label="C42_C_0402_1005Metric_86d094c5ae72"
  LinkPlacement = pos=(32.61,-32.455,0) rot=(0,0,1;0rad)
  LinkedObject = -> Shape001
  Placement = pos=(32.61,-32.455,0) rot=(0,0,1;0rad)
FEATURE [App::Link] C81_C_0402_1005Metric_8f684d3886a5_ln_054  label="C21_C_0402_1005Metric_922c465759c3"
  LinkPlacement = pos=(6.59145,8.3,0) rot=(0,0,1;0.785398rad)
  LinkedObject = -> Shape001
  Placement = pos=(6.59145,8.3,0) rot=(0,0,1;0.785398rad)
FEATURE [App::Link] R14_R_0402_1005Metric_de650128e65b_ln_037  label="R52_R_0402_1005Metric_0677dc0bfb77"
  LinkPlacement = pos=(20.475,-15.28,0) rot=(0,0,1;1.5708rad)
  LinkedObject = -> Shape
  Placement = pos=(20.475,-15.28,0) rot=(0,0,1;1.5708rad)
FEATURE [App::Link] R14_R_0402_1005Metric_de650128e65b_ln_038  label="R20_R_0402_1005Metric_cd89faa0d0ef"
  LinkPlacement = pos=(-22.85,-17.89,0) rot=(0,0,-1;1.5708rad)
  LinkedObject = -> Shape
  Placement = pos=(-22.85,-17.89,0) rot=(0,0,-1;1.5708rad)
FEATURE [App::Link] R14_R_0402_1005Metric_de650128e65b_ln_039  label="R71_R_0402_1005Metric_c4f40f2a7a7f"
  LinkPlacement = pos=(-9.78,18.5398,0) rot=(0,0,-1;1.5708rad)
  LinkedObject = -> Shape
  Placement = pos=(-9.78,18.5398,0) rot=(0,0,-1;1.5708rad)
FEATURE [App::Link] C81_C_0402_1005Metric_8f684d3886a5_ln_055  label="C129_C_0402_1005Metric_1b858f0f78b6"
  LinkPlacement = pos=(-16.2,-31.6,0) rot=(0,0,1;0rad)
  LinkedObject = -> Shape001
  Placement = pos=(-16.2,-31.6,0) rot=(0,0,1;0rad)
FEATURE [App::Link] R14_R_0402_1005Metric_de650128e65b_ln_040  label="R3_R_0402_1005Metric_8f3d4db6a679"
  LinkPlacement = pos=(-21.65,-17.9,0) rot=(0,0,1;1.5708rad)
  LinkedObject = -> Shape
  Placement = pos=(-21.65,-17.9,0) rot=(0,0,1;1.5708rad)
FEATURE [App::Link] C81_C_0402_1005Metric_8f684d3886a5_ln_056  label="C126_C_0402_1005Metric_cd4063b6522c"
  LinkPlacement = pos=(-27.825,-32.46,0) rot=(0,0,1;0rad)
  LinkedObject = -> Shape001
  Placement = pos=(-27.825,-32.46,0) rot=(0,0,1;0rad)
FEATURE [App::Link] C81_C_0402_1005Metric_8f684d3886a5_ln_057  label="C125_C_0402_1005Metric_fd6dff404434"
  LinkPlacement = pos=(-16.195,-29.3,0) rot=(0,0,1;0rad)
  LinkedObject = -> Shape001
  Placement = pos=(-16.195,-29.3,0) rot=(0,0,1;0rad)
FEATURE [App::Link] R14_R_0402_1005Metric_de650128e65b_ln_041  label="R49_R_0402_1005Metric_384648d3a73e"
  LinkPlacement = pos=(10.8,-32.96,0) rot=(0,0,1;1.5708rad)
  LinkedObject = -> Shape
  Placement = pos=(10.8,-32.96,0) rot=(0,0,1;1.5708rad)
FEATURE [App::Link] C81_C_0402_1005Metric_8f684d3886a5_ln_058  label="C95_C_0402_1005Metric_e176ad0f7dd1"
  LinkPlacement = pos=(-0.125001,-34.68,0) rot=(0,0,-1;1.5708rad)
  LinkedObject = -> Shape001
  Placement = pos=(-0.125001,-34.68,0) rot=(0,0,-1;1.5708rad)
FEATURE [App::Link] C81_C_0402_1005Metric_8f684d3886a5_ln_059  label="C104_C_0402_1005Metric_6dcc717ee803"
  LinkPlacement = pos=(-8.85,-25.685,0) rot=(0,0,1;3.14159rad)
  LinkedObject = -> Shape001
  Placement = pos=(-8.85,-25.685,0) rot=(0,0,1;3.14159rad)
FEATURE [App::Link] R14_R_0402_1005Metric_de650128e65b_ln_042  label="R61_R_0402_1005Metric_308f9ddf36ab"
  LinkPlacement = pos=(-3.325,-23.375,0) rot=(0,0,1;1.5708rad)
  LinkedObject = -> Shape
  Placement = pos=(-3.325,-23.375,0) rot=(0,0,1;1.5708rad)
FEATURE [App::Link] C11_C_0603_1608Metric_4ead5bbb98ed_ln_003  label="C147_C_0603_1608Metric_314164621751"
  LinkPlacement = pos=(0.604036,8.16988,0) rot=(0,0,1;3.92699rad)
  LinkedObject = -> Shape005
  Placement = pos=(0.604036,8.16988,0) rot=(0,0,1;3.92699rad)
FEATURE [App::Link] C81_C_0402_1005Metric_8f684d3886a5_ln_060  label="C91_C_0402_1005Metric_c4f385c02458"
  LinkPlacement = pos=(-10.475,-28.53,0) rot=(0,0,-1;1.5708rad)
  LinkedObject = -> Shape001
  Placement = pos=(-10.475,-28.53,0) rot=(0,0,-1;1.5708rad)
FEATURE [App::Link] R14_R_0402_1005Metric_de650128e65b_ln_043  label="R6_R_0402_1005Metric_30edd58b5cf5"
  LinkPlacement = pos=(37.2,-17.92,0) rot=(0,0,1;1.5708rad)
  LinkedObject = -> Shape
  Placement = pos=(37.2,-17.92,0) rot=(0,0,1;1.5708rad)
FEATURE [App::Link] C81_C_0402_1005Metric_8f684d3886a5_ln_061  label="C43_C_0402_1005Metric_d14d6348d082"
  LinkPlacement = pos=(39.25,-34.67,0) rot=(0,0,-1;1.5708rad)
  LinkedObject = -> Shape001
  Placement = pos=(39.25,-34.67,0) rot=(0,0,-1;1.5708rad)
FEATURE [App::Link] C81_C_0402_1005Metric_8f684d3886a5_ln_062  label="C5_C_0402_1005Metric_e8aaf7cac2ab"
  LinkPlacement = pos=(31.6,11.2,0) rot=(0,0,-1;1.5708rad)
  LinkedObject = -> Shape001
  Placement = pos=(31.6,11.2,0) rot=(0,0,-1;1.5708rad)
FEATURE [App::Link] C81_C_0402_1005Metric_8f684d3886a5_ln_063  label="C138_C_0402_1005Metric_28c44dda1afc"
  LinkPlacement = pos=(-27.82,-30.26,0) rot=(0,0,1;3.14159rad)
  LinkedObject = -> Shape001
  Placement = pos=(-27.82,-30.26,0) rot=(0,0,1;3.14159rad)
FEATURE [App::Link] R14_R_0402_1005Metric_de650128e65b_ln_044  label="R21_R_0402_1005Metric_97da80f97d13"
  LinkPlacement = pos=(6.01,18.4148,0) rot=(0,0,1;3.14159rad)
  LinkedObject = -> Shape
  Placement = pos=(6.01,18.4148,0) rot=(0,0,1;3.14159rad)
FEATURE [App::Link] C81_C_0402_1005Metric_8f684d3886a5_ln_064  label="C50_C_0402_1005Metric_44ec480db2bf"
  LinkPlacement = pos=(44.2,-30.57,0) rot=(0,0,1;0rad)
  LinkedObject = -> Shape001
  Placement = pos=(44.2,-30.57,0) rot=(0,0,1;0rad)
FEATURE [App::Link] C81_C_0402_1005Metric_8f684d3886a5_ln_065  label="C34_C_0402_1005Metric_f1ae7a0c68ec"
  LinkPlacement = pos=(36.525,-33.565,0) rot=(0,0,-1;1.5708rad)
  LinkedObject = -> Shape001
  Placement = pos=(36.525,-33.565,0) rot=(0,0,-1;1.5708rad)
FEATURE [App::Link] C81_C_0402_1005Metric_8f684d3886a5_ln_066  label="C90_C_0402_1005Metric_895964040edd"
  LinkPlacement = pos=(-3.8,-33.565,0) rot=(0,0,-1;1.5708rad)
  LinkedObject = -> Shape001
  Placement = pos=(-3.8,-33.565,0) rot=(0,0,-1;1.5708rad)
FEATURE [App::Link] C81_C_0402_1005Metric_8f684d3886a5_ln_067  label="C154_C_0402_1005Metric_1cbc4a6436a7"
  LinkPlacement = pos=(-13.35,-14.91,0) rot=(0,0,1;3.14159rad)
  LinkedObject = -> Shape001
  Placement = pos=(-13.35,-14.91,0) rot=(0,0,1;3.14159rad)
FEATURE [App::Link] C81_C_0402_1005Metric_8f684d3886a5_ln_068  label="C41_C_0402_1005Metric_16070ec987db"
  LinkPlacement = pos=(44.21,-29.3,0) rot=(0,0,1;0rad)
  LinkedObject = -> Shape001
  Placement = pos=(44.21,-29.3,0) rot=(0,0,1;0rad)
FEATURE [App::Link] R14_R_0402_1005Metric_de650128e65b_ln_045  label="R40_R_0402_1005Metric_df3cfc33963d"
  LinkPlacement = pos=(44.3,-17.9,0) rot=(0,0,-1;1.5708rad)
  LinkedObject = -> Shape
  Placement = pos=(44.3,-17.9,0) rot=(0,0,-1;1.5708rad)
FEATURE [App::Link] C81_C_0402_1005Metric_8f684d3886a5_ln_069  label="C23_C_0402_1005Metric_4b9de6996c17"
  LinkPlacement = pos=(20.8644,13.4644,0) rot=(0,0,1;0.785398rad)
  LinkedObject = -> Shape001
  Placement = pos=(20.8644,13.4644,0) rot=(0,0,1;0.785398rad)
FEATURE [App::Link] R14_R_0402_1005Metric_de650128e65b_ln_046  label="R31_R_0402_1005Metric_d878a7efed0c"
  LinkPlacement = pos=(34.95,11.69,0) rot=(0,0,1;3.14159rad)
  LinkedObject = -> Shape
  Placement = pos=(34.95,11.69,0) rot=(0,0,1;3.14159rad)
FEATURE [App::Link] C81_C_0402_1005Metric_8f684d3886a5_ln_070  label="C25_C_0402_1005Metric_13517506eb46"
  LinkPlacement = pos=(5.31263,11.2573,0) rot=(0,0,1;2.35619rad)
  LinkedObject = -> Shape001
  Placement = pos=(5.31263,11.2573,0) rot=(0,0,1;2.35619rad)
FEATURE [App::Link] R14_R_0402_1005Metric_de650128e65b_ln_047  label="R62_R_0402_1005Metric_07fa69280419"
  LinkPlacement = pos=(-15.125,-17.885,0) rot=(0,0,-1;1.5708rad)
  LinkedObject = -> Shape
  Placement = pos=(-15.125,-17.885,0) rot=(0,0,-1;1.5708rad)
FEATURE [App::Link] R14_R_0402_1005Metric_de650128e65b_ln_048  label="R27_R_0402_1005Metric_41c2b4cdfe8d"
  LinkPlacement = pos=(23.5,21.2,0) rot=(0,0,-1;1.5708rad)
  LinkedObject = -> Shape
  Placement = pos=(23.5,21.2,0) rot=(0,0,-1;1.5708rad)
FEATURE [App::Link] R14_R_0402_1005Metric_de650128e65b_ln_049  label="R11_R_0402_1005Metric_774c97bf6f02"
  LinkPlacement = pos=(-5.325,-17.9,0) rot=(0,0,1;1.5708rad)
  LinkedObject = -> Shape
  Placement = pos=(-5.325,-17.9,0) rot=(0,0,1;1.5708rad)
FEATURE [Part::Feature] Shape013  label="J8_SM08B-SRSS_a19acebb16da[2]"
  Placement = pos=(6.62,25.9948,-0.3) rot=(0,0.707107,0.707107;3.14159rad)
  shape: bbox 10 x 4.95 x 2.96 mm, 133 faces (baked)
FEATURE [App::Link] C81_C_0402_1005Metric_8f684d3886a5_ln_071  label="C8_C_0402_1005Metric_4136ac707e2d"
  LinkPlacement = pos=(1.73941,-2.06059,0) rot=(0,0,1;0.785398rad)
  LinkedObject = -> Shape001
  Placement = pos=(1.73941,-2.06059,0) rot=(0,0,1;0.785398rad)
FEATURE [App::Link] R14_R_0402_1005Metric_de650128e65b_ln_050  label="R58_R_0402_1005Metric_bd763b63da8d"
  LinkPlacement = pos=(-8.85,-24.56,0) rot=(0,0,1;3.14159rad)
  LinkedObject = -> Shape
  Placement = pos=(-8.85,-24.56,0) rot=(0,0,1;3.14159rad)
FEATURE [App::Link] C81_C_0402_1005Metric_8f684d3886a5_ln_072  label="C66_C_0402_1005Metric_8d50cf637d0f"
  LinkPlacement = pos=(15.775,-23.375,0) rot=(0,0,1;1.5708rad)
  LinkedObject = -> Shape001
  Placement = pos=(15.775,-23.375,0) rot=(0,0,1;1.5708rad)
FEATURE [App::Link] C81_C_0402_1005Metric_8f684d3886a5_ln_073  label="C77_C_0402_1005Metric_2777696603b7"
  LinkPlacement = pos=(18.2,-23.385,0) rot=(0,0,1;1.5708rad)
  LinkedObject = -> Shape001
  Placement = pos=(18.2,-23.385,0) rot=(0,0,1;1.5708rad)
FEATURE [App::Link] C81_C_0402_1005Metric_8f684d3886a5_ln_074  label="C143_C_0402_1005Metric_8f43f1f19f21"
  LinkPlacement = pos=(-23.125,-38.03,0) rot=(0,0,-1;1.5708rad)
  LinkedObject = -> Shape001
  Placement = pos=(-23.125,-38.03,0) rot=(0,0,-1;1.5708rad)
FEATURE [App::Link] SW2_EVQPU_LC_02K_v4_ac6ec0e7e283_2__ln_  label="SW1_EVQPU-LC-02K v4_2906fa296057[2]"
  LinkPlacement = pos=(41.45,0.700001,0) rot=(0.57735,0.57735,0.57735;2.0944rad)
  LinkedObject = -> Shape008
  Placement = pos=(41.45,0.700001,0) rot=(0.57735,0.57735,0.57735;2.0944rad)
FEATURE [App::Link] C81_C_0402_1005Metric_8f684d3886a5_ln_075  label="C99_C_0402_1005Metric_bdcbd65efbb5"
  LinkPlacement = pos=(-1.15,-34.68,0) rot=(0,0,-1;1.5708rad)
  LinkedObject = -> Shape001
  Placement = pos=(-1.15,-34.68,0) rot=(0,0,-1;1.5708rad)
FEATURE [App::Link] R14_R_0402_1005Metric_de650128e65b_ln_051  label="R65_R_0402_1005Metric_ad31060daa5e"
  LinkPlacement = pos=(-29.425,-32.935,0) rot=(0,0,1;1.5708rad)
  LinkedObject = -> Shape
  Placement = pos=(-29.425,-32.935,0) rot=(0,0,1;1.5708rad)
FEATURE [App::Link] C81_C_0402_1005Metric_8f684d3886a5_ln_076  label="C26_C_0402_1005Metric_a3132ec88abe"
  LinkPlacement = pos=(27.002,-0.307107,0) rot=(0,0,-1;0.785398rad)
  LinkedObject = -> Shape001
  Placement = pos=(27.002,-0.307107,0) rot=(0,0,-1;0.785398rad)
FEATURE [App::Link] R14_R_0402_1005Metric_de650128e65b_ln_052  label="R7_R_0402_1005Metric_e4d857eaf7f4"
  LinkPlacement = pos=(35.975,-17.92,0) rot=(0,0,1;1.5708rad)
  LinkedObject = -> Shape
  Placement = pos=(35.975,-17.92,0) rot=(0,0,1;1.5708rad)
FEATURE [App::Link] C81_C_0402_1005Metric_8f684d3886a5_ln_077  label="C145_C_0402_1005Metric_4a45116d8563"
  LinkPlacement = pos=(10.22,-20.05,0) rot=(0,0,1;0rad)
  LinkedObject = -> Shape001
  Placement = pos=(10.22,-20.05,0) rot=(0,0,1;0rad)
FEATURE [App::Link] C81_C_0402_1005Metric_8f684d3886a5_ln_078  label="C122_C_0402_1005Metric_7a2c3fd7bf36"
  LinkPlacement = pos=(-24.425,-23.38,0) rot=(0,0,1;1.5708rad)
  LinkedObject = -> Shape001
  Placement = pos=(-24.425,-23.38,0) rot=(0,0,1;1.5708rad)
FEATURE [App::Link] C81_C_0402_1005Metric_8f684d3886a5_ln_079  label="C128_C_0402_1005Metric_5ac61b07c1cb"
  LinkPlacement = pos=(-27.82,-31.36,0) rot=(0,0,1;3.14159rad)
  LinkedObject = -> Shape001
  Placement = pos=(-27.82,-31.36,0) rot=(0,0,1;3.14159rad)
FEATURE [App::Link] C81_C_0402_1005Metric_8f684d3886a5_ln_080  label="C6_C_0402_1005Metric_e1363baee549"
  LinkPlacement = pos=(11.4697,17.4394,0) rot=(0,0,-1;0.785398rad)
  LinkedObject = -> Shape001
  Placement = pos=(11.4697,17.4394,0) rot=(0,0,-1;0.785398rad)
FEATURE [App::Link] C11_C_0603_1608Metric_4ead5bbb98ed_ln_004  label="C27_C_0603_1608Metric_47e074de3aa9"
  LinkPlacement = pos=(3.06462,9.40531,0) rot=(0,0,1;2.35619rad)
  LinkedObject = -> Shape005
  Placement = pos=(3.06462,9.40531,0) rot=(0,0,1;2.35619rad)
FEATURE [App::Link] R14_R_0402_1005Metric_de650128e65b_ln_053  label="R79_R_0402_1005Metric_a0183a2d3266"
  LinkPlacement = pos=(31.2375,-17.86,0) rot=(0,0,-1;1.5708rad)
  LinkedObject = -> Shape
  Placement = pos=(31.2375,-17.86,0) rot=(0,0,-1;1.5708rad)
FEATURE [App::Link] C11_C_0603_1608Metric_4ead5bbb98ed_ln_005  label="C89_C_0603_1608Metric_49bbeca9b139"
  LinkPlacement = pos=(2.225,-34.76,0) rot=(0,0,-1;1.5708rad)
  LinkedObject = -> Shape005
  Placement = pos=(2.225,-34.76,0) rot=(0,0,-1;1.5708rad)
FEATURE [App::Link] U5_QFN40P600X600X90_48_Nordic_Semiconductor_QFN48_2cf8b7c55fc9_ln_001  label="U9_QFN40P600X600X90-48_Nordic_Semiconductor_QFN48_80ca248f0380"
  LinkPlacement = pos=(-21.675,-28.76,0) rot=(0,0,1;0rad)
  LinkedObject = -> Shape009
  Placement = pos=(-21.675,-28.76,0) rot=(0,0,1;0rad)
FEATURE [App::Link] R14_R_0402_1005Metric_de650128e65b_ln_054  label="R1_R_0402_1005Metric_fff765507076"
  LinkPlacement = pos=(34.1725,24.85,0) rot=(0,0,1;3.14159rad)
  LinkedObject = -> Shape
  Placement = pos=(34.1725,24.85,0) rot=(0,0,1;3.14159rad)
FEATURE [App::Link] D20_SOT_886_1dd8b907bd9e_ln_001  label="D21_SOT_886_7ec86c1c348b"
  LinkPlacement = pos=(8.11,20.4898,0) rot=(0,0,1;0rad)
  LinkedObject = -> Shape006
  Placement = pos=(8.11,20.4898,0) rot=(0,0,1;0rad)
FEATURE [App::Link] C81_C_0402_1005Metric_8f684d3886a5_ln_081  label="C153_C_0402_1005Metric_b86b98a15c3a"
  LinkPlacement = pos=(26.7375,-14.91,0) rot=(0,0,1;3.14159rad)
  LinkedObject = -> Shape001
  Placement = pos=(26.7375,-14.91,0) rot=(0,0,1;3.14159rad)
FEATURE [App::Link] C81_C_0402_1005Metric_8f684d3886a5_ln_082  label="C137_C_0402_1005Metric_ece53a7faaec"
  LinkPlacement = pos=(-16.2,-27.92,0) rot=(0,0,1;0rad)
  LinkedObject = -> Shape001
  Placement = pos=(-16.2,-27.92,0) rot=(0,0,1;0rad)
FEATURE [App::Link] R14_R_0402_1005Metric_de650128e65b_ln_055  label="R9_R_0402_1005Metric_56e936c92618"
  LinkPlacement = pos=(-24.05,-17.9,0) rot=(0,0,1;1.5708rad)
  LinkedObject = -> Shape
  Placement = pos=(-24.05,-17.9,0) rot=(0,0,1;1.5708rad)
FEATURE [App::Link] C81_C_0402_1005Metric_8f684d3886a5_ln_083  label="C46_C_0402_1005Metric_4d31e522836d"
  LinkPlacement = pos=(40.68,-33.2,0) rot=(0,0,1;0rad)
  LinkedObject = -> Shape001
  Placement = pos=(40.68,-33.2,0) rot=(0,0,1;0rad)
FEATURE [App::Link] R14_R_0402_1005Metric_de650128e65b_ln_056  label="R34_R_0402_1005Metric_be70cc6bbce9"
  LinkPlacement = pos=(-24.55,16.25,0) rot=(0,0,1;3.14159rad)
  LinkedObject = -> Shape
  Placement = pos=(-24.55,16.25,0) rot=(0,0,1;3.14159rad)
FEATURE [App::Link] R14_R_0402_1005Metric_de650128e65b_ln_057  label="R24_R_0402_1005Metric_0dcc0f07c909"
  LinkPlacement = pos=(22,21.1598,0) rot=(0,0,1;1.5708rad)
  LinkedObject = -> Shape
  Placement = pos=(22,21.1598,0) rot=(0,0,1;1.5708rad)
FEATURE [App::Link] C81_C_0402_1005Metric_8f684d3886a5_ln_084  label="C133_C_0402_1005Metric_b8dc1c093e78"
  LinkPlacement = pos=(-21.975,-23.39,0) rot=(0,0,1;1.5708rad)
  LinkedObject = -> Shape001
  Placement = pos=(-21.975,-23.39,0) rot=(0,0,1;1.5708rad)
FEATURE [App::Link] C81_C_0402_1005Metric_8f684d3886a5_ln_085  label="C132_C_0402_1005Metric_cb599351975c"
  LinkPlacement = pos=(-28.975,-25.685,0) rot=(0,0,1;3.14159rad)
  LinkedObject = -> Shape001
  Placement = pos=(-28.975,-25.685,0) rot=(0,0,1;3.14159rad)
FEATURE [App::Link] R14_R_0402_1005Metric_de650128e65b_ln_058  label="R67_R_0402_1005Metric_f7b376ffc9f0"
  LinkPlacement = pos=(-18.025,-15.28,0) rot=(0,0,1;1.5708rad)
  LinkedObject = -> Shape
  Placement = pos=(-18.025,-15.28,0) rot=(0,0,1;1.5708rad)
FEATURE [App::Link] C81_C_0402_1005Metric_8f684d3886a5_ln_086  label="C19_C_0402_1005Metric_7e0bbb8ef52f"
  LinkPlacement = pos=(21.625,12.7,0) rot=(0,0,1;0.785398rad)
  LinkedObject = -> Shape001
  Placement = pos=(21.625,12.7,0) rot=(0,0,1;0.785398rad)
FEATURE [App::Link] D13_LED_0603_1608Metric_a9e6ce14452c_ln_008  label="D15_LED_0603_1608Metric_05a7a2657bbb"
  LinkPlacement = pos=(-18.025,-17.92,0) rot=(0,0,-1;1.5708rad)
  LinkedObject = -> Shape003
  Placement = pos=(-18.025,-17.92,0) rot=(0,0,-1;1.5708rad)
FEATURE [App::Link] R14_R_0402_1005Metric_de650128e65b_ln_059  label="R16_R_0402_1005Metric_da0392fd5641"
  LinkPlacement = pos=(18.4,-17.92,0) rot=(0,0,-1;1.5708rad)
  LinkedObject = -> Shape
  Placement = pos=(18.4,-17.92,0) rot=(0,0,-1;1.5708rad)
FEATURE [App::Link] D20_SOT_886_1dd8b907bd9e_ln_002  label="D5_SOT_886_c9ec05460939"
  LinkPlacement = pos=(26.75,-8.65,0) rot=(0,0,1;3.92699rad)
  LinkedObject = -> Shape006
  Placement = pos=(26.75,-8.65,0) rot=(0,0,1;3.92699rad)
FEATURE [App::Link] C81_C_0402_1005Metric_8f684d3886a5_ln_087  label="C10_C_0402_1005Metric_9a3b4b04c936"
  LinkPlacement = pos=(-18.25,12.23,0) rot=(0,0,1;1.5708rad)
  LinkedObject = -> Shape001
  Placement = pos=(-18.25,12.23,0) rot=(0,0,1;1.5708rad)
FEATURE [App::Link] C81_C_0402_1005Metric_8f684d3886a5_ln_088  label="C44_C_0402_1005Metric_c0a448a9726b"
  LinkPlacement = pos=(32.6,-31.36,0) rot=(0,0,1;3.14159rad)
  LinkedObject = -> Shape001
  Placement = pos=(32.6,-31.36,0) rot=(0,0,1;3.14159rad)
FEATURE [Part::Feature] Part__Feature018  label="A(V)TX-13"
  shape: bbox 2 x 0.75 x 1.6 mm, 68 faces (baked)
FEATURE [Part::Feature] Part__Feature019  label="A(V)TX-014"
  shape: bbox 0.1906 x 0.001 x 0.2 mm, 15 faces (baked)
FEATURE [Part::Feature] Part__Feature020  label="A(V)TX-015"
  shape: bbox 0.1919 x 0.001 x 0.2 mm, 11 faces (baked)
FEATURE [Part::Feature] Part__Feature021  label="A(V)TX-016"
  shape: bbox 0.06667 x 0.001 x 0.2538 mm, 11 faces (baked)
FEATURE [Part::Feature] Part__Feature022  label="A(V)TX-017"
  shape: bbox 0.1821 x 0.001 x 0.2 mm, 18 faces (baked)
FEATURE [Part::Feature] Part__Feature023  label="A(V)TX-018"
  shape: bbox 1.8 x 0.05 x 1.4 mm, 10 faces (baked)
FEATURE [Part::Feature] Part__Feature024  label="A(V)TX-019"
  shape: bbox 0.0718 x 0.001 x 0.2 mm, 9 faces (baked)
FEATURE [Part::Feature] Part__Feature025  label="A(V)TX-020"
  shape: bbox 0.65 x 0.3 x 0.55 mm, 10 faces (baked)
FEATURE [Part::Feature] Part__Feature026  label="A(V)TX-021"
  shape: bbox 0.65 x 0.3 x 0.55 mm, 9 faces (baked)
FEATURE [Part::Feature] Part__Feature027  label="A(V)TX-022"
  shape: bbox 0.65 x 0.3 x 0.55 mm, 9 faces (baked)
FEATURE [Part::Feature] Part__Feature028  label="A(V)TX-023"
  shape: bbox 0.65 x 0.3 x 0.55 mm, 9 faces (baked)
FEATURE [Part::Feature] Part__Feature029  label="A(V)TX-024"
  shape: bbox 0.06667 x 0.001 x 0.2538 mm, 11 faces (baked)
FEATURE [Part::Feature] Part__Feature030  label="A(V)TX-025"
  shape: bbox 0.125 x 0.001 x 0.125 mm, 4 faces (baked)
FEATURE [Part::Feature] Part__Feature031  label="A(V)TX-026"
  shape: bbox 0.1564 x 0.001 x 0.2 mm, 10 faces (baked)
FEATURE [Part::Feature] Part__Feature032  label="A(V)TX-027"
  shape: bbox 0.07436 x 0.001 x 0.02308 mm, 6 faces (baked)
FEATURE [Part::Feature] Part__Feature033  label="A(V)TX-028"
  shape: bbox 0.1282 x 0.001 x 0.2026 mm, 19 faces (baked)
FEATURE [App::Part] A_V_TX_13  label="U11_A(V)TX-029_3b5ddad8c5aa"
  Group = -> [Part__Feature018,Part__Feature019,Part__Feature020,Part__Feature021,Part__Feature022,Part__Feature023,Part__Feature024,Part__Feature025,Part__Feature026,Part__Feature027,Part__Feature028,Part__Feature029,Part__Feature030,Part__Feature031,Part__Feature032,Part__Feature033]
  Origin = -> Origin012
  Placement = pos=(10.2,-17.6,0) rot=(0.57735,0.57735,0.57735;2.0944rad)
FEATURE [App::Link] L1_L_0402_1005Metric_5998b2d09642_ln_  label="L2_L_0402_1005Metric_79f78b55d2f9"
  LinkPlacement = pos=(-0.8,0.215847,0) rot=(0,0,-1;0.785398rad)
  LinkedObject = -> Shape010
  Placement = pos=(-0.8,0.215847,0) rot=(0,0,-1;0.785398rad)
FEATURE [Part::Feature] Part__Feature034  label="Body"
  Placement = pos=(0,0,0.1) rot=(0,0,1;0rad)
  shape: bbox 2.6 x 2.4 x 1.1 mm, 6 faces (baked)
FEATURE [Part::Feature] Part__Feature035  label="Pins"
  shape: bbox 0.755 x 0.48 x 0.1 mm, 6 faces (baked)
FEATURE [Part::Feature] Part__Feature036  label="Pins001"
  shape: bbox 0.755 x 0.48 x 0.1 mm, 6 faces (baked)
FEATURE [Part::Feature] Part__Feature037  label="Pins002"
  shape: bbox 0.755 x 0.48 x 0.1 mm, 6 faces (baked)
FEATURE [Part::Feature] Part__Feature038  label="Pins003"
  shape: bbox 0.755 x 0.48 x 0.1 mm, 6 faces (baked)
FEATURE [App::Part] Pins  label="Pins004"
  Group = -> [Part__Feature035,Part__Feature036,Part__Feature037,Part__Feature038]
  Origin = -> Origin013
FEATURE [App::Part] ASSEMBLY  label="D7_ASSEMBLY_e1df3af2d95e[2]"
  Group = -> [Part__Feature034,Pins]
  Origin = -> Origin014
  Placement = pos=(36.9125,15.6,0) rot=(0,0,-1;1.5708rad)
FEATURE [Part::Feature] Shape014  label="L3_L_0603_1608Metric_e494f57d1672"
  Placement = pos=(2.90889,6.86105,0) rot=(0,0,1;2.35619rad)
  shape: bbox 1.697 x 1.697 x 0.8 mm, 28 faces (baked)
FEATURE [App::Link] R14_R_0402_1005Metric_de650128e65b_ln_060  label="R38_R_0402_1005Metric_7cbdb940c1f9"
  LinkPlacement = pos=(45.5,-17.91,0) rot=(0,0,-1;1.5708rad)
  LinkedObject = -> Shape
  Placement = pos=(45.5,-17.91,0) rot=(0,0,-1;1.5708rad)
FEATURE [App::Link] C81_C_0402_1005Metric_8f684d3886a5_ln_089  label="C20_C_0402_1005Metric_26da8f60711b"
  LinkPlacement = pos=(7.61263,-4.52152,0) rot=(0,0,1;3.92699rad)
  LinkedObject = -> Shape001
  Placement = pos=(7.61263,-4.52152,0) rot=(0,0,1;3.92699rad)
FEATURE [App::Link] U5_QFN40P600X600X90_48_Nordic_Semiconductor_QFN48_2cf8b7c55fc9_ln_002  label="U3_QFN40P600X600X90-48_Nordic_Semiconductor_QFN48_1b4446f60428"
  LinkPlacement = pos=(38.725,-28.785,0) rot=(0,0,1;0rad)
  LinkedObject = -> Shape009
  Placement = pos=(38.725,-28.785,0) rot=(0,0,1;0rad)
FEATURE [App::Link] C11_C_0603_1608Metric_4ead5bbb98ed_ln_006  label="C33_C_0603_1608Metric_e09c2b669a15"
  LinkPlacement = pos=(42.55,-34.76,0) rot=(0,0,-1;1.5708rad)
  LinkedObject = -> Shape005
  Placement = pos=(42.55,-34.76,0) rot=(0,0,-1;1.5708rad)
FEATURE [App::Link] R14_R_0402_1005Metric_de650128e65b_ln_061  label="R64_R_0402_1005Metric_4f40dbadbd75"
  LinkPlacement = pos=(-16.375,-17.88,0) rot=(0,0,-1;1.5708rad)
  LinkedObject = -> Shape
  Placement = pos=(-16.375,-17.88,0) rot=(0,0,-1;1.5708rad)
FEATURE [App::Link] R14_R_0402_1005Metric_de650128e65b_ln_062  label="R17_R_0402_1005Metric_0cc88b999155"
  LinkPlacement = pos=(-4.15,-17.9,0) rot=(0,0,-1;1.5708rad)
  LinkedObject = -> Shape
  Placement = pos=(-4.15,-17.9,0) rot=(0,0,-1;1.5708rad)
FEATURE [App::Link] C81_C_0402_1005Metric_8f684d3886a5_ln_090  label="C49_C_0402_1005Metric_99bb872bd996"
  LinkPlacement = pos=(38.4,-23.385,0) rot=(0,0,1;1.5708rad)
  LinkedObject = -> Shape001
  Placement = pos=(38.4,-23.385,0) rot=(0,0,1;1.5708rad)
FEATURE [App::Link] R14_R_0402_1005Metric_de650128e65b_ln_063  label="R44_R_0402_1005Metric_4f91b837a811"
  LinkPlacement = pos=(40.65,-15.28,0) rot=(0,0,1;1.5708rad)
  LinkedObject = -> Shape
  Placement = pos=(40.65,-15.28,0) rot=(0,0,1;1.5708rad)
FEATURE [App::Link] R14_R_0402_1005Metric_de650128e65b_ln_064  label="R10_R_0402_1005Metric_97514c00872a"
  LinkPlacement = pos=(0.15,-8.4,0) rot=(0,0,-1;1.5708rad)
  LinkedObject = -> Shape
  Placement = pos=(0.15,-8.4,0) rot=(0,0,-1;1.5708rad)
FEATURE [App::Link] C81_C_0402_1005Metric_8f684d3886a5_ln_091  label="C71_C_0402_1005Metric_e526097947d7"
  LinkPlacement = pos=(18.99,-34.68,0) rot=(0,0,-1;1.5708rad)
  LinkedObject = -> Shape001
  Placement = pos=(18.99,-34.68,0) rot=(0,0,-1;1.5708rad)
FEATURE [App::Link] R14_R_0402_1005Metric_de650128e65b_ln_065  label="R59_R_0402_1005Metric_9715952a53a7"
  LinkPlacement = pos=(2.075,-15.28,0) rot=(0,0,1;1.5708rad)
  LinkedObject = -> Shape
  Placement = pos=(2.075,-15.28,0) rot=(0,0,1;1.5708rad)
FEATURE [App::Link] C81_C_0402_1005Metric_8f684d3886a5_ln_092  label="C121_C_0402_1005Metric_016f9ca88e31"
  LinkPlacement = pos=(-19.2,-34.67,0) rot=(0,0,-1;1.5708rad)
  LinkedObject = -> Shape001
  Placement = pos=(-19.2,-34.67,0) rot=(0,0,-1;1.5708rad)
FEATURE [App::Link] R14_R_0402_1005Metric_de650128e65b_ln_066  label="R26_R_0402_1005Metric_c57c44c8c734"
  LinkPlacement = pos=(33.8625,15.55,0) rot=(0,0,1;3.14159rad)
  LinkedObject = -> Shape
  Placement = pos=(33.8625,15.55,0) rot=(0,0,1;3.14159rad)
FEATURE [App::Link] C81_C_0402_1005Metric_8f684d3886a5_ln_093  label="C24_C_0402_1005Metric_6f5cbd21e82e"
  LinkPlacement = pos=(11.852,-8.78211,0) rot=(0,0,1;3.92699rad)
  LinkedObject = -> Shape001
  Placement = pos=(11.852,-8.78211,0) rot=(0,0,1;3.92699rad)
FEATURE [App::Link] R14_R_0402_1005Metric_de650128e65b_ln_067  label="R51_R_0402_1005Metric_c1a8e2f8916b"
  LinkPlacement = pos=(22.15,-15.28,0) rot=(0,0,1;1.5708rad)
  LinkedObject = -> Shape
  Placement = pos=(22.15,-15.28,0) rot=(0,0,1;1.5708rad)
FEATURE [App::Link] C81_C_0402_1005Metric_8f684d3886a5_ln_094  label="C112_C_0402_1005Metric_1ee4088cbbe5"
  LinkPlacement = pos=(-5.425,-23.38,0) rot=(0,0,1;1.5708rad)
  LinkedObject = -> Shape001
  Placement = pos=(-5.425,-23.38,0) rot=(0,0,1;1.5708rad)
FEATURE [Part::Feature] Part__Feature039  label="MPM3610 v2"
  shape: bbox 0.9 x 0.21 x 1.95 mm, 14 faces (baked)
FEATURE [Part::Feature] Part__Feature040  label="MPM3610 v003"
  shape: bbox 0.25 x 0.21 x 0.4 mm, 6 faces (baked)
FEATURE [Part::Feature] Part__Feature041  label="MPM3610 v004"
  shape: bbox 0.8 x 0.21 x 0.25 mm, 6 faces (baked)
FEATURE [Part::Feature] Part__Feature042  label="MPM3610 v005"
  shape: bbox 0.5 x 0.21 x 0.25 mm, 7 faces (baked)
FEATURE [Part::Feature] Part__Feature043  label="MPM3610 v006"
  shape: bbox 0.25 x 0.21 x 0.4 mm, 6 faces (baked)
FEATURE [Part::Feature] Part__Feature044  label="MPM3610 v007"
  shape: bbox 0.25 x 0.21 x 0.4 mm, 6 faces (baked)
FEATURE [Part::Feature] Part__Feature045  label="MPM3610 v008"
  shape: bbox 0.4 x 0.21 x 0.25 mm, 6 faces (baked)
FEATURE [Part::Feature] Part__Feature046  label="MPM3610 v009"
  shape: bbox 0.8 x 0.21 x 0.25 mm, 6 faces (baked)
FEATURE [Part::Feature] Part__Feature047  label="MPM3610 v010"
  shape: bbox 0.25 x 0.21 x 0.8 mm, 6 faces (baked)
FEATURE [Part::Feature] Part__Feature048  label="MPM3610 v011"
  shape: bbox 0.8 x 0.21 x 0.25 mm, 6 faces (baked)
FEATURE [Part::Feature] Part__Feature049  label="MPM3610 v012"
  shape: bbox 0.8 x 0.21 x 1.95 mm, 14 faces (baked)
FEATURE [Part::Feature] Part__Feature050  label="MPM3610 v013"
  shape: bbox 0.25 x 0.21 x 0.4 mm, 6 faces (baked)
FEATURE [Part::Feature] Part__Feature051  label="MPM3610 v014"
  shape: bbox 0.25 x 0.21 x 0.8 mm, 6 faces (baked)
FEATURE [Part::Feature] Part__Feature052  label="MPM3610 v015"
  shape: bbox 0.8 x 0.21 x 0.25 mm, 6 faces (baked)
FEATURE [Part::Feature] Part__Feature053  label="MPM3610 v016"
  shape: bbox 0.2 x 0.01 x 0.2 mm, 3 faces (baked)
FEATURE [Part::Feature] Part__Feature054  label="MPM3610 v017"
  shape: bbox 3 x 1.5 x 5 mm, 79 faces (baked)
FEATURE [App::Part] MPM3610_v2  label="U2_MPM3610 v018_523d3ef717d7"
  Group = -> [Part__Feature039,Part__Feature040,Part__Feature041,Part__Feature042,Part__Feature043,Part__Feature044,Part__Feature045,Part__Feature046,Part__Feature047,Part__Feature048,Part__Feature049,Part__Feature050,Part__Feature051,Part__Feature052,Part__Feature053,Part__Feature054]
  Origin = -> Origin015
  Placement = pos=(-21.55,12.3,0) rot=(1,0,0;1.5708rad)
FEATURE [App::Link] C81_C_0402_1005Metric_8f684d3886a5_ln_095  label="C4_C_0402_1005Metric_dab9d57a4135"
  LinkPlacement = pos=(-21.33,16.75,0) rot=(0,0,1;0rad)
  LinkedObject = -> Shape001
  Placement = pos=(-21.33,16.75,0) rot=(0,0,1;0rad)
FEATURE [App::Link] C81_C_0402_1005Metric_8f684d3886a5_ln_096  label="C96_C_0402_1005Metric_d77f652d8b78"
  LinkPlacement = pos=(-6.1,-32.91,0) rot=(0,0,1;1.5708rad)
  LinkedObject = -> Shape001
  Placement = pos=(-6.1,-32.91,0) rot=(0,0,1;1.5708rad)
FEATURE [Part::Feature] Part__Feature055  label="part004"
  shape: bbox 0.16 x 0.16 x 0.002 mm, 3 faces (baked)
FEATURE [Part::Feature] Part__Feature056  label="part005"
  shape: bbox 3.2 x 2.49 x 0.807 mm, 6 faces (baked)
FEATURE [Part::Feature] Part__Feature057  label="part006"
  shape: bbox 1.295 x 2.49 x 0.006 mm, 6 faces (baked)
FEATURE [Part::Feature] Part__Feature058  label="part007"
  shape: bbox 1.295 x 2.49 x 0.006 mm, 6 faces (baked)
FEATURE [App::Part] part001  label="Y1_part008_91518c197ebe"
  Group = -> [Part__Feature055,Part__Feature056,Part__Feature057,Part__Feature058]
  Origin = -> Origin016
  Placement = pos=(9.65204,14.9179,0) rot=(0,0,1;0.785398rad)
FEATURE [Part::Feature] Shape015  label="U13_SOT_23_6_3c237a761f51"
  Placement = pos=(30.0875,-14.9,0) rot=(0,0,1;3.14159rad)
  shape: bbox 2.8 x 2.9 x 1.55 mm, 124 faces (baked)
FEATURE [App::Link] C81_C_0402_1005Metric_8f684d3886a5_ln_097  label="C63_C_0402_1005Metric_24c12ad7c640"
  LinkPlacement = pos=(9.65,-28.53,0) rot=(0,0,-1;1.5708rad)
  LinkedObject = -> Shape001
  Placement = pos=(9.65,-28.53,0) rot=(0,0,-1;1.5708rad)
FEATURE [App::Link] C81_C_0402_1005Metric_8f684d3886a5_ln_098  label="C140_C_0402_1005Metric_e1ecbd19dbc4"
  LinkPlacement = pos=(-23.875,-33.565,0) rot=(0,0,-1;1.5708rad)
  LinkedObject = -> Shape001
  Placement = pos=(-23.875,-33.565,0) rot=(0,0,-1;1.5708rad)
FEATURE [App::Link] C81_C_0402_1005Metric_8f684d3886a5_ln_099  label="C119_C_0402_1005Metric_2fd261537f44"
  LinkPlacement = pos=(-30.575,-28.53,0) rot=(0,0,-1;1.5708rad)
  LinkedObject = -> Shape001
  Placement = pos=(-30.575,-28.53,0) rot=(0,0,-1;1.5708rad)
FEATURE [App::Link] R14_R_0402_1005Metric_de650128e65b_ln_068  label="R36_R_0402_1005Metric_aae624751809"
  LinkPlacement = pos=(-24.95,14.36,0) rot=(0,0,1;1.5708rad)
  LinkedObject = -> Shape
  Placement = pos=(-24.95,14.36,0) rot=(0,0,1;1.5708rad)
FEATURE [App::Link] C81_C_0402_1005Metric_8f684d3886a5_ln_100  label="C106_C_0402_1005Metric_ea553233606d"
  LinkPlacement = pos=(3.895,-30.56,0) rot=(0,0,1;0rad)
  LinkedObject = -> Shape001
  Placement = pos=(3.895,-30.56,0) rot=(0,0,1;0rad)
FEATURE [App::Link] D13_LED_0603_1608Metric_a9e6ce14452c_ln_009  label="D11_LED_0603_1608Metric_7eee010ddfe1"
  LinkPlacement = pos=(22.15,-17.92,0) rot=(0,0,-1;1.5708rad)
  LinkedObject = -> Shape003
  Placement = pos=(22.15,-17.92,0) rot=(0,0,-1;1.5708rad)
FEATURE [App::Link] R14_R_0402_1005Metric_de650128e65b_ln_069  label="R12_R_0402_1005Metric_60fa6b75f90e"
  LinkPlacement = pos=(34.1775,21.1,0) rot=(0,0,1;3.14159rad)
  LinkedObject = -> Shape
  Placement = pos=(34.1775,21.1,0) rot=(0,0,1;3.14159rad)
FEATURE [App::Link] R14_R_0402_1005Metric_de650128e65b_ln_070  label="R56_R_0402_1005Metric_999ef0e664ad"
  LinkPlacement = pos=(3.85,-17.88,0) rot=(0,0,-1;1.5708rad)
  LinkedObject = -> Shape
  Placement = pos=(3.85,-17.88,0) rot=(0,0,-1;1.5708rad)
FEATURE [App::Link] C81_C_0402_1005Metric_8f684d3886a5_ln_101  label="C85_C_0402_1005Metric_6792222946b0"
  LinkPlacement = pos=(19.275,-23.405,0) rot=(0,0,1;1.5708rad)
  LinkedObject = -> Shape001
  Placement = pos=(19.275,-23.405,0) rot=(0,0,1;1.5708rad)
FEATURE [App::Link] C81_C_0402_1005Metric_8f684d3886a5_ln_102  label="C13_C_0402_1005Metric_dadf54943dae"
  LinkPlacement = pos=(1.75204,2.51789,0) rot=(0,0,1;2.35619rad)
  LinkedObject = -> Shape001
  Placement = pos=(1.75204,2.51789,0) rot=(0,0,1;2.35619rad)
FEATURE [App::Link] C81_C_0402_1005Metric_8f684d3886a5_ln_103  label="C101_C_0402_1005Metric_91740c9b690b"
  LinkPlacement = pos=(3.885,-31.6,0) rot=(0,0,1;0rad)
  LinkedObject = -> Shape001
  Placement = pos=(3.885,-31.6,0) rot=(0,0,1;0rad)
FEATURE [App::Link] C81_C_0402_1005Metric_8f684d3886a5_ln_104  label="C18_C_0402_1005Metric_bb7f6a42ce3b"
  LinkPlacement = pos=(25.2415,-2.07152,0) rot=(0,0,-1;0.785398rad)
  LinkedObject = -> Shape001
  Placement = pos=(25.2415,-2.07152,0) rot=(0,0,-1;0.785398rad)
FEATURE [App::Link] R14_R_0402_1005Metric_de650128e65b_ln_071  label="R53_R_0402_1005Metric_0b88a59c23a8"
  LinkPlacement = pos=(16.825,-23.375,0) rot=(0,0,1;1.5708rad)
  LinkedObject = -> Shape
  Placement = pos=(16.825,-23.375,0) rot=(0,0,1;1.5708rad)
FEATURE [App::Link] C11_C_0603_1608Metric_4ead5bbb98ed_ln_007  label="C12_C_0603_1608Metric_8525907a5b0f"
  LinkPlacement = pos=(0.304036,1.5659,0) rot=(0,0,1;2.35619rad)
  LinkedObject = -> Shape005
  Placement = pos=(0.304036,1.5659,0) rot=(0,0,1;2.35619rad)
FEATURE [App::Link] C81_C_0402_1005Metric_8f684d3886a5_ln_105  label="C118_C_0402_1005Metric_026764cf1bef"
  LinkPlacement = pos=(-25.45,-23.38,0) rot=(0,0,1;1.5708rad)
  LinkedObject = -> Shape001
  Placement = pos=(-25.45,-23.38,0) rot=(0,0,1;1.5708rad)
FEATURE [App::Link] R14_R_0402_1005Metric_de650128e65b_ln_072  label="R33_R_0402_1005Metric_32bc5c120f6b"
  LinkPlacement = pos=(-24.56,17.65,0) rot=(0,0,1;0rad)
  LinkedObject = -> Shape
  Placement = pos=(-24.56,17.65,0) rot=(0,0,1;0rad)
FEATURE [App::Link] C81_C_0402_1005Metric_8f684d3886a5_ln_106  label="C36_C_0402_1005Metric_558d1c522963"
  LinkPlacement = pos=(29.74,-30.46,0) rot=(0,0,-1;1.5708rad)
  LinkedObject = -> Shape001
  Placement = pos=(29.74,-30.46,0) rot=(0,0,-1;1.5708rad)
FEATURE [App::Link] J6_U_FL_Hirose_U_FL_R_SMT_1_Vertical_4116725bd3ca_ln_002  label="J5_U.FL_Hirose_U.FL-R-SMT-1_Vertical_18b22338faa5"
  LinkPlacement = pos=(-1.75,-45.785,0) rot=(0,0,-1;1.5708rad)
  LinkedObject = -> Shape012
  Placement = pos=(-1.75,-45.785,0) rot=(0,0,-1;1.5708rad)
FEATURE [App::Link] C81_C_0402_1005Metric_8f684d3886a5_ln_107  label="C94_C_0402_1005Metric_141206e406dc"
  LinkPlacement = pos=(-4.375,-23.38,0) rot=(0,0,1;1.5708rad)
  LinkedObject = -> Shape001
  Placement = pos=(-4.375,-23.38,0) rot=(0,0,1;1.5708rad)
FEATURE [App::Link] C81_C_0402_1005Metric_8f684d3886a5_ln_108  label="C37_C_0402_1005Metric_f812b44437f8"
  LinkPlacement = pos=(41.25,-34.67,0) rot=(0,0,-1;1.5708rad)
  LinkedObject = -> Shape001
  Placement = pos=(41.25,-34.67,0) rot=(0,0,-1;1.5708rad)
FEATURE [App::Link] C81_C_0402_1005Metric_8f684d3886a5_ln_109  label="C70_C_0402_1005Metric_51cc4e54c910"
  LinkPlacement = pos=(12.4,-32.455,0) rot=(0,0,1;0rad)
  LinkedObject = -> Shape001
  Placement = pos=(12.4,-32.455,0) rot=(0,0,1;0rad)
FEATURE [App::Link] R14_R_0402_1005Metric_de650128e65b_ln_073  label="R13_R_0402_1005Metric_65859b9f1d11"
  LinkPlacement = pos=(34.1775,19.2,0) rot=(0,0,1;3.14159rad)
  LinkedObject = -> Shape
  Placement = pos=(34.1775,19.2,0) rot=(0,0,1;3.14159rad)
FEATURE [App::Link] C11_C_0603_1608Metric_4ead5bbb98ed_ln_008  label="C2_C_0603_1608Metric_04b0ad459168"
  LinkPlacement = pos=(-21.025,18.45,0) rot=(0,0,1;0rad)
  LinkedObject = -> Shape005
  Placement = pos=(-21.025,18.45,0) rot=(0,0,1;0rad)
FEATURE [App::Link] C81_C_0402_1005Metric_8f684d3886a5_ln_110  label="C58_C_0402_1005Metric_a62a94538538"
  LinkPlacement = pos=(38.575,-38.03,0) rot=(0,0,-1;1.5708rad)
  LinkedObject = -> Shape001
  Placement = pos=(38.575,-38.03,0) rot=(0,0,-1;1.5708rad)
FEATURE [App::Link] C81_C_0402_1005Metric_8f684d3886a5_ln_111  label="C116_C_0402_1005Metric_a94416a5297c"
  LinkPlacement = pos=(-28.975,-29,0) rot=(0,0,1;3.14159rad)
  LinkedObject = -> Shape001
  Placement = pos=(-28.975,-29,0) rot=(0,0,1;3.14159rad)
FEATURE [App::Link] C81_C_0402_1005Metric_8f684d3886a5_ln_112  label="C152_C_0402_1005Metric_74aa059ddaa4"
  LinkPlacement = pos=(-13.35,-13.8,0) rot=(0,0,1;3.14159rad)
  LinkedObject = -> Shape001
  Placement = pos=(-13.35,-13.8,0) rot=(0,0,1;3.14159rad)
FEATURE [App::Link] R14_R_0402_1005Metric_de650128e65b_ln_074  label="R82_R_0402_1005Metric_a457e30b783c"
  LinkPlacement = pos=(-11.15,-17.86,0) rot=(0,0,-1;1.5708rad)
  LinkedObject = -> Shape
  Placement = pos=(-11.15,-17.86,0) rot=(0,0,-1;1.5708rad)
FEATURE [App::Link] C81_C_0402_1005Metric_8f684d3886a5_ln_113  label="C35_C_0402_1005Metric_9cf1c69fe912"
  LinkPlacement = pos=(29.74,-28.52,0) rot=(0,0,-1;1.5708rad)
  LinkedObject = -> Shape001
  Placement = pos=(29.74,-28.52,0) rot=(0,0,-1;1.5708rad)
FEATURE [App::Link] C81_C_0402_1005Metric_8f684d3886a5_ln_114  label="C39_C_0402_1005Metric_c03e2536d7ae"
  LinkPlacement = pos=(40.25,-34.67,0) rot=(0,0,-1;1.5708rad)
  LinkedObject = -> Shape001
  Placement = pos=(40.25,-34.67,0) rot=(0,0,-1;1.5708rad)
FEATURE [App::Link] R14_R_0402_1005Metric_de650128e65b_ln_075  label="R69_R_0402_1005Metric_976a0127df7d"
  LinkPlacement = pos=(-23.375,-23.39,0) rot=(0,0,1;1.5708rad)
  LinkedObject = -> Shape
  Placement = pos=(-23.375,-23.39,0) rot=(0,0,1;1.5708rad)
FEATURE [App::Link] C81_C_0402_1005Metric_8f684d3886a5_ln_115  label="C57_C_0402_1005Metric_446286936caa"
  LinkPlacement = pos=(39.475,-23.405,0) rot=(0,0,1;1.5708rad)
  LinkedObject = -> Shape001
  Placement = pos=(39.475,-23.405,0) rot=(0,0,1;1.5708rad)
FEATURE [App::Link] U13_SOT_23_6_3c237a761f51_ln_  label="U14_SOT_23_6_b9ac4dee4ad5"
  LinkPlacement = pos=(-10,-14.9,0) rot=(0,0,1;3.14159rad)
  LinkedObject = -> Shape015
  Placement = pos=(-10,-14.9,0) rot=(0,0,1;3.14159rad)
FEATURE [App::Link] C81_C_0402_1005Metric_8f684d3886a5_ln_116  label="C31_C_0402_1005Metric_523f556ad02e"
  LinkPlacement = pos=(23.1144,11.2144,0) rot=(0,0,1;0.785398rad)
  LinkedObject = -> Shape001
  Placement = pos=(23.1144,11.2144,0) rot=(0,0,1;0.785398rad)
FEATURE [App::Link] R14_R_0402_1005Metric_de650128e65b_ln_076  label="R19_R_0402_1005Metric_9d85d64749f0"
  LinkPlacement = pos=(38.4,-17.92,0) rot=(0,0,-1;1.5708rad)
  LinkedObject = -> Shape
  Placement = pos=(38.4,-17.92,0) rot=(0,0,-1;1.5708rad)
FEATURE [App::Link] C81_C_0402_1005Metric_8f684d3886a5_ln_117  label="C82_C_0402_1005Metric_0037f3eb8195"
  LinkPlacement = pos=(12.4,-30.26,0) rot=(0,0,1;3.14159rad)
  LinkedObject = -> Shape001
  Placement = pos=(12.4,-30.26,0) rot=(0,0,1;3.14159rad)
FEATURE [App::Link] R14_R_0402_1005Metric_de650128e65b_ln_077  label="R5_R_0402_1005Metric_1ff1049ddc9e"
  LinkPlacement = pos=(16,-17.9,0) rot=(0,0,1;1.5708rad)
  LinkedObject = -> Shape
  Placement = pos=(16,-17.9,0) rot=(0,0,1;1.5708rad)
FEATURE [App::Link] D13_LED_0603_1608Metric_a9e6ce14452c_ln_010  label="D3_LED_0603_1608Metric_ff6d41324402"
  LinkPlacement = pos=(36.9125,21.1,0) rot=(0,0,1;0rad)
  LinkedObject = -> Shape003
  Placement = pos=(36.9125,21.1,0) rot=(0,0,1;0rad)
FEATURE [App::Link] R14_R_0402_1005Metric_de650128e65b_ln_078  label="R48_R_0402_1005Metric_d1f9b8e5bb5d"
  LinkPlacement = pos=(23.95,-17.88,0) rot=(0,0,-1;1.5708rad)
  LinkedObject = -> Shape
  Placement = pos=(23.95,-17.88,0) rot=(0,0,-1;1.5708rad)
FEATURE [App::Link] C81_C_0402_1005Metric_8f684d3886a5_ln_118  label="C40_C_0402_1005Metric_c81de3bdeb78"
  LinkPlacement = pos=(34.24,-32.93,0) rot=(0,0,1;1.5708rad)
  LinkedObject = -> Shape001
  Placement = pos=(34.24,-32.93,0) rot=(0,0,1;1.5708rad)
FEATURE [App::Link] C81_C_0402_1005Metric_8f684d3886a5_ln_119  label="C123_C_0402_1005Metric_7f8ca1308ae8"
  LinkPlacement = pos=(-20.225,-34.67,0) rot=(0,0,-1;1.5708rad)
  LinkedObject = -> Shape001
  Placement = pos=(-20.225,-34.67,0) rot=(0,0,-1;1.5708rad)
FEATURE [App::Link] D13_LED_0603_1608Metric_a9e6ce14452c_ln_011  label="D1_LED_0603_1608Metric_8a8584d3a0c4"
  LinkPlacement = pos=(36.9,24.85,0) rot=(0,0,1;0rad)
  LinkedObject = -> Shape003
  Placement = pos=(36.9,24.85,0) rot=(0,0,1;0rad)
FEATURE [App::Link] C81_C_0402_1005Metric_8f684d3886a5_ln_120  label="C45_C_0402_1005Metric_a7227102ca7b"
  LinkPlacement = pos=(44.2,-31.6,0) rot=(0,0,1;0rad)
  LinkedObject = -> Shape001
  Placement = pos=(44.2,-31.6,0) rot=(0,0,1;0rad)
FEATURE [App::Link] R14_R_0402_1005Metric_de650128e65b_ln_079  label="R55_R_0402_1005Metric_29c292d169c4"
  LinkPlacement = pos=(-7.25,-28.5,0) rot=(0,0,1;1.5708rad)
  LinkedObject = -> Shape
  Placement = pos=(-7.25,-28.5,0) rot=(0,0,1;1.5708rad)
FEATURE [App::Link] C81_C_0402_1005Metric_8f684d3886a5_ln_121  label="C76_C_0402_1005Metric_43a29dbd9ad4"
  LinkPlacement = pos=(11.25,-25.71,0) rot=(0,0,1;3.14159rad)
  LinkedObject = -> Shape001
  Placement = pos=(11.25,-25.71,0) rot=(0,0,1;3.14159rad)
FEATURE [App::Link] C81_C_0402_1005Metric_8f684d3886a5_ln_122  label="C87_C_0402_1005Metric_51c5b427e19f"
  LinkPlacement = pos=(17.075,-38.03,0) rot=(0,0,-1;1.5708rad)
  LinkedObject = -> Shape001
  Placement = pos=(17.075,-38.03,0) rot=(0,0,-1;1.5708rad)
FEATURE [App::Link] C81_C_0402_1005Metric_8f684d3886a5_ln_123  label="C15_C_0402_1005Metric_9169a4dcd3b4"
  LinkPlacement = pos=(2.59146,3.37848,0) rot=(0,0,1;2.35619rad)
  LinkedObject = -> Shape001
  Placement = pos=(2.59146,3.37848,0) rot=(0,0,1;2.35619rad)
FEATURE [App::Link] C81_C_0402_1005Metric_8f684d3886a5_ln_124  label="C142_C_0402_1005Metric_d2cb65e0ba8d"
  LinkPlacement = pos=(-21.825,-38.03,0) rot=(0,0,-1;1.5708rad)
  LinkedObject = -> Shape001
  Placement = pos=(-21.825,-38.03,0) rot=(0,0,-1;1.5708rad)
FEATURE [App::Link] C11_C_0603_1608Metric_4ead5bbb98ed_ln_009  label="C14_C_0603_1608Metric_dad5bcacfcf7"
  LinkPlacement = pos=(17.802,15.3139,0) rot=(0,0,1;2.35619rad)
  LinkedObject = -> Shape005
  Placement = pos=(17.802,15.3139,0) rot=(0,0,1;2.35619rad)
FEATURE [App::Link] C81_C_0402_1005Metric_8f684d3886a5_ln_125  label="C110_C_0402_1005Metric_7d2bc15bb31b"
  LinkPlacement = pos=(-7.695,-30.26,0) rot=(0,0,1;3.14159rad)
  LinkedObject = -> Shape001
  Placement = pos=(-7.695,-30.26,0) rot=(0,0,1;3.14159rad)
FEATURE [App::Link] R14_R_0402_1005Metric_de650128e65b_ln_080  label="R77_R_0402_1005Metric_9e5c0c89f6fc"
  LinkPlacement = pos=(10.8,-14.57,0) rot=(0,0,-1;1.5708rad)
  LinkedObject = -> Shape
  Placement = pos=(10.8,-14.57,0) rot=(0,0,-1;1.5708rad)
FEATURE [App::Link] C81_C_0402_1005Metric_8f684d3886a5_ln_126  label="C64_C_0402_1005Metric_7ff52b14e7e8"
  LinkPlacement = pos=(9.65,-30.46,0) rot=(0,0,-1;1.5708rad)
  LinkedObject = -> Shape001
  Placement = pos=(9.65,-30.46,0) rot=(0,0,-1;1.5708rad)
FEATURE [App::Link] C81_C_0402_1005Metric_8f684d3886a5_ln_127  label="C67_C_0402_1005Metric_44ec82e10a5d"
  LinkPlacement = pos=(20,-34.68,0) rot=(0,0,-1;1.5708rad)
  LinkedObject = -> Shape001
  Placement = pos=(20,-34.68,0) rot=(0,0,-1;1.5708rad)
FEATURE [App::Link] C81_C_0402_1005Metric_8f684d3886a5_ln_128  label="C7_C_0402_1005Metric_a28f265bd716"
  LinkPlacement = pos=(7.01974,12.9894,0) rot=(0,0,-1;0.785398rad)
  LinkedObject = -> Shape001
  Placement = pos=(7.01974,12.9894,0) rot=(0,0,-1;0.785398rad)
FEATURE [App::Part] Top_b912
  Group = -> [Shape,Shape001,R14_R_0402_1005Metric_de650128e65b_ln_,R14_R_0402_1005Metric_de650128e65b_ln_001,Shape002,C81_C_0402_1005Metric_8f684d3886a5_ln_,C81_C_0402_1005Metric_8f684d3886a5_ln_001,R14_R_0402_1005Metric_de650128e65b_ln_002,R14_R_0402_1005Metric_de650128e65b_ln_003,R14_R_0402_1005Metric_de650128e65b_ln_004,R14_R_0402_1005Metric_de650128e65b_ln_005,Shape003,+257 more]
  Origin = -> Origin003
FEATURE [Part::Feature] Shape016  label="R85_C_0805_2012Metric_1fa3b4aae098"
  Placement = pos=(28.95,-14.95,-1.58) rot=(0.707107,-0.707107,0;3.14159rad)
  shape: bbox 1.25 x 2 x 1.25 mm, 28 faces (baked)
FEATURE [App::Link] C81_C_0402_1005Metric_8f684d3886a5_ln_129  label="C108_C_0402_1005Metric_ba19ef845f69"
  LinkPlacement = pos=(-0.125001,-34.68,-1.58) rot=(0.707107,-0.707107,0;3.14159rad)
  LinkedObject = -> Shape001
  Placement = pos=(-0.125001,-34.68,-1.58) rot=(0.707107,-0.707107,0;3.14159rad)
FEATURE [App::Link] C81_C_0402_1005Metric_8f684d3886a5_ln_130  label="C103_C_0402_1005Metric_865c6c595753"
  LinkPlacement = pos=(0.899999,-34.68,-1.58) rot=(0.707107,-0.707107,0;3.14159rad)
  LinkedObject = -> Shape001
  Placement = pos=(0.899999,-34.68,-1.58) rot=(0.707107,-0.707107,0;3.14159rad)
FEATURE [App::Link] C81_C_0402_1005Metric_8f684d3886a5_ln_131  label="C83_C_0402_1005Metric_6ef42dc9aa70"
  LinkPlacement = pos=(18.99,-34.68,-1.58) rot=(0.707107,-0.707107,0;3.14159rad)
  LinkedObject = -> Shape001
  Placement = pos=(18.99,-34.68,-1.58) rot=(0.707107,-0.707107,0;3.14159rad)
FEATURE [App::Link] C81_C_0402_1005Metric_8f684d3886a5_ln_132  label="C111_C_0402_1005Metric_3f28c6da6f33"
  LinkPlacement = pos=(-1.15,-34.68,-1.58) rot=(0.707107,-0.707107,0;3.14159rad)
  LinkedObject = -> Shape001
  Placement = pos=(-1.15,-34.68,-1.58) rot=(0.707107,-0.707107,0;3.14159rad)
FEATURE [App::Link] C81_C_0402_1005Metric_8f684d3886a5_ln_133  label="C80_C_0402_1005Metric_98df26384085"
  LinkPlacement = pos=(20,-34.68,-1.58) rot=(0.707107,-0.707107,0;3.14159rad)
  LinkedObject = -> Shape001
  Placement = pos=(20,-34.68,-1.58) rot=(0.707107,-0.707107,0;3.14159rad)
FEATURE [App::Link] C81_C_0402_1005Metric_8f684d3886a5_ln_134  label="C52_C_0402_1005Metric_430faeccbc77"
  LinkPlacement = pos=(40.25,-34.67,-1.58) rot=(0.707107,-0.707107,0;3.14159rad)
  LinkedObject = -> Shape001
  Placement = pos=(40.25,-34.67,-1.58) rot=(0.707107,-0.707107,0;3.14159rad)
FEATURE [App::Link] C81_C_0402_1005Metric_8f684d3886a5_ln_135  label="C136_C_0402_1005Metric_4945e57dee50"
  LinkPlacement = pos=(-20.225,-34.67,-1.58) rot=(0.707107,-0.707107,0;3.14159rad)
  LinkedObject = -> Shape001
  Placement = pos=(-20.225,-34.67,-1.58) rot=(0.707107,-0.707107,0;3.14159rad)
FEATURE [App::Link] C81_C_0402_1005Metric_8f684d3886a5_ln_136  label="C75_C_0402_1005Metric_384e78777628"
  LinkPlacement = pos=(21,-34.685,-1.58) rot=(0.707107,-0.707107,0;3.14159rad)
  LinkedObject = -> Shape001
  Placement = pos=(21,-34.685,-1.58) rot=(0.707107,-0.707107,0;3.14159rad)
FEATURE [App::Link] R85_C_0805_2012Metric_1fa3b4aae098_ln_  label="R84_C_0805_2012Metric_9030c96586ab"
  LinkPlacement = pos=(31.25,-14.95,-1.58) rot=(0.707107,-0.707107,0;3.14159rad)
  LinkedObject = -> Shape016
  Placement = pos=(31.25,-14.95,-1.58) rot=(0.707107,-0.707107,0;3.14159rad)
FEATURE [App::Link] R85_C_0805_2012Metric_1fa3b4aae098_ln_001  label="R87_C_0805_2012Metric_cdb49fc28253"
  LinkPlacement = pos=(-11.2,-14.95,-1.58) rot=(0.707107,-0.707107,0;3.14159rad)
  LinkedObject = -> Shape016
  Placement = pos=(-11.2,-14.95,-1.58) rot=(0.707107,-0.707107,0;3.14159rad)
FEATURE [App::Link] C81_C_0402_1005Metric_8f684d3886a5_ln_137  label="C55_C_0402_1005Metric_96c38573c253"
  LinkPlacement = pos=(39.25,-34.67,-1.58) rot=(0.707107,-0.707107,0;3.14159rad)
  LinkedObject = -> Shape001
  Placement = pos=(39.25,-34.67,-1.58) rot=(0.707107,-0.707107,0;3.14159rad)
FEATURE [App::Link] R85_C_0805_2012Metric_1fa3b4aae098_ln_002  label="R83_C_0805_2012Metric_a20fdbddcdcd"
  LinkPlacement = pos=(-5.1,-7.9,-1.58) rot=(0.707107,-0.707107,0;3.14159rad)
  LinkedObject = -> Shape016
  Placement = pos=(-5.1,-7.9,-1.58) rot=(0.707107,-0.707107,0;3.14159rad)
FEATURE [App::Link] C81_C_0402_1005Metric_8f684d3886a5_ln_138  label="C47_C_0402_1005Metric_9e700e8794ea"
  LinkPlacement = pos=(41.25,-34.67,-1.58) rot=(0.707107,-0.707107,0;3.14159rad)
  LinkedObject = -> Shape001
  Placement = pos=(41.25,-34.67,-1.58) rot=(0.707107,-0.707107,0;3.14159rad)
FEATURE [App::Link] C81_C_0402_1005Metric_8f684d3886a5_ln_139  label="C131_C_0402_1005Metric_db240f167f28"
  LinkPlacement = pos=(-19.2,-34.67,-1.58) rot=(0.707107,-0.707107,0;3.14159rad)
  LinkedObject = -> Shape001
  Placement = pos=(-19.2,-34.67,-1.58) rot=(0.707107,-0.707107,0;3.14159rad)
FEATURE [App::Link] C81_C_0402_1005Metric_8f684d3886a5_ln_140  label="C139_C_0402_1005Metric_824a71a4541d"
  LinkPlacement = pos=(-21.25,-34.67,-1.58) rot=(0.707107,-0.707107,0;3.14159rad)
  LinkedObject = -> Shape001
  Placement = pos=(-21.25,-34.67,-1.58) rot=(0.707107,-0.707107,0;3.14159rad)
FEATURE [App::Link] R85_C_0805_2012Metric_1fa3b4aae098_ln_003  label="R86_C_0805_2012Metric_4fbc304b175e"
  LinkPlacement = pos=(-8.9,-14.95,-1.58) rot=(0.707107,-0.707107,0;3.14159rad)
  LinkedObject = -> Shape016
  Placement = pos=(-8.9,-14.95,-1.58) rot=(0.707107,-0.707107,0;3.14159rad)
FEATURE [App::Part] Bot_b912
  Group = -> [Shape016,C81_C_0402_1005Metric_8f684d3886a5_ln_129,C81_C_0402_1005Metric_8f684d3886a5_ln_130,C81_C_0402_1005Metric_8f684d3886a5_ln_131,C81_C_0402_1005Metric_8f684d3886a5_ln_132,C81_C_0402_1005Metric_8f684d3886a5_ln_133,C81_C_0402_1005Metric_8f684d3886a5_ln_134,C81_C_0402_1005Metric_8f684d3886a5_ln_135,C81_C_0402_1005Metric_8f684d3886a5_ln_136,R85_C_0805_2012Metric_1fa3b4aae098_ln_,+7 more]
  Origin = -> Origin004
FEATURE [App::Part] Step_Models_b912
  Group = -> [Top_b912,Bot_b912]
  Origin = -> Origin002
FEATURE [Part::Feature] pads_area286001  label="topPads_b912"
  Placement = pos=(-58.8,135.6,0.02) rot=(0,0,1;0rad)
  shape: bbox 80.4 x 80.4 x 2e-07 mm, 1684 faces, 0 solids (baked)
FEATURE [Part::Feature] Shape017001  label="topTracks_b912"
  Placement = pos=(-58.8,135.6,0.01) rot=(0,0,1;0rad)
  shape: bbox 77.73 x 71.61 x 2e-07 mm, 377 faces, 0 solids (baked)
FEATURE [Part::Feature] zones_area001  label="topZones_b912"
  Placement = pos=(-58.8,135.6,0.01) rot=(0,0,1;0rad)
  shape: bbox 82.54 x 82.57 x 2e-07 mm, 30 faces, 0 solids (baked)
FEATURE [Part::Feature] pads_area286071001  label="botPads_b912"
  Placement = pos=(-58.8,135.6,-1.6) rot=(0,0,1;0rad)
  shape: bbox 80.4 x 80.4 x 2e-07 mm, 808 faces, 0 solids (baked)
FEATURE [Part::Feature] Shape017002001  label="botTracks_b912"
  Placement = pos=(-58.8,135.6,-1.59) rot=(0,0,1;0rad)
  shape: bbox 74.45 x 62.83 x 2e-07 mm, 111 faces, 0 solids (baked)
FEATURE [Part::Feature] zones_area002001  label="botZones_b912"
  Placement = pos=(-58.8,135.6,-1.59) rot=(0,0,1;0rad)
  shape: bbox 82.54 x 82.57 x 2e-07 mm, 16 faces, 0 solids (baked)
FEATURE [App::Part] Board_Geoms_b912
  Group = -> [Pcb_b912,PCB_Sketch_b912,pads_area286001,Shape017001,zones_area001,pads_area286071001,Shape017002001,zones_area002001]
  Origin = -> Origin
FEATURE [App::Part] Board_b912  label="ReLoki_ECAD"
  Group = -> [Local_CS_b912,Board_Geoms_b912,Step_Models_b912]
  Origin = -> Origin001
